FCSTD DOCUMENT  (FreeCAD 1.0R39109 (Git))
Label: CenterCoil
License: All rights reserved
LicenseURL: http://en.wikipedia.org/wiki/All_rights_reserved
objects: Sketcher::SketchObject×84, PartDesign::Pocket×55, PartDesign::Pad×22, PartDesign::PolarPattern×14, PartDesign::Body×10, App::Part×9, PartDesign::Chamfer×9, PartDesign::Fillet×8, PartDesign::Groove×5, Part::Feature×3, PartDesign::SubtractiveHelix×1
note: 509 computed .brp shape members not serialized (recipe doc carries the construction recipe); baked Part::Feature solids carry a one-line shape summary decoded from their .brp

FEATURE [Sketcher::SketchObject] Sketch
  ArcFitTolerance = 1e-06
  AttachmentSupport = -> [XY_Plane001]
  FullyConstrained = true
  MakeInternals = false
  MapMode = 5
  sketch-geometry (1):
    g0: Circle CenterX=0 CenterY=0 CenterZ=0 NormalX=0 NormalY=0 NormalZ=1 AngleXU=0 Radius=38.1
  constraints (2):
    c: Diameter(g0) = 76.2
    c: Coincident(g0,g-1)
FEATURE [PartDesign::Pad] Pad  label="CoilPad"
  Direction = (0,0,1)
  Length = 101.15
  Length2 = 10
  Profile = -> Sketch
  ReferenceAxis = -> Sketch [N_Axis]
  Suppressed = false
  Type = 0
FEATURE [Sketcher::SketchObject] Sketch001
  ArcFitTolerance = 1e-06
  AttachmentSupport = -> [XZ_Plane001]
  FullyConstrained = true
  MakeInternals = false
  MapMode = 5
  Placement = pos=(0,0,0) rot=(1,0,0;1.5708rad)
  sketch-geometry (1):
    g0: Circle CenterX=38.1 CenterY=4 CenterZ=0 NormalX=0 NormalY=0 NormalZ=1 AngleXU=0 Radius=1
  constraints (3):
    c: Diameter(g0) = 2
    c: DistanceX(g-1,g0) = 38.1
    c: DistanceY(g-1,g0) = 4
FEATURE [PartDesign::SubtractiveHelix] SubtractiveHelix
  Angle = 0
  Axis = (0,2e-16,1)
  Base = (0,0,0)
  BaseFeature = -> Pad
  Growth = 0
  HasBeenEdited = true
  Height = 93.15
  LeftHanded = false
  Mode = 0
  Outside = false
  Pitch = 2.3
  Profile = -> Sketch001
  ReferenceAxis = -> Sketch001 [V_Axis]
  Suppressed = false
  Tolerance = 0.1
  Turns = 40.5
FEATURE [Sketcher::SketchObject] Sketch002
  ArcFitTolerance = 1e-06
  AttachmentSupport = -> [SubtractiveHelix]
  FullyConstrained = true
  MakeInternals = false
  MapMode = 5
  Placement = pos=(0,0,101.15) rot=(0,0,1;0rad)
  sketch-geometry (1):
    g0: Circle CenterX=0 CenterY=0 CenterZ=0 NormalX=0 NormalY=0 NormalZ=1 AngleXU=0 Radius=23.1
  constraints (2):
    c: Diameter(g0) = 46.2
    c: Coincident(g0,g-1)
FEATURE [PartDesign::Pocket] Pocket  label="CenterPocket"
  BaseFeature = -> SubtractiveHelix
  Direction = (0,0,-1)
  Length = 5
  Length2 = 5
  Profile = -> Sketch002
  ReferenceAxis = -> Sketch002 [N_Axis]
  Suppressed = false
  Type = 1
FEATURE [Sketcher::SketchObject] Sketch003
  ArcFitTolerance = 1e-06
  AttachmentSupport = -> [Pocket]
  FullyConstrained = true
  MakeInternals = false
  MapMode = 5
  Placement = pos=(0,0,101.15) rot=(0,0,1;0rad)
  sketch-geometry (1):
    g0: Circle CenterX=0 CenterY=30.06 CenterZ=0 NormalX=0 NormalY=0 NormalZ=1 AngleXU=0 Radius=3.3
  constraints (3):
    c: Diameter(g0) = 6.6
    c: PointOnObject(g0,g-2)
    c: DistanceY(g-1,g0) = 30.06
FEATURE [PartDesign::Pocket] Pocket001  label="TopScrewPocket"
  BaseFeature = -> Pocket
  Direction = (0,0,-1)
  Length = 20
  Length2 = 5
  Profile = -> Sketch003
  ReferenceAxis = -> Sketch003 [N_Axis]
  Suppressed = false
  Type = 0
FEATURE [PartDesign::PolarPattern] PolarPattern  label="TopScrewPolarPattern"
  Angle = 360
  Axis = -> Sketch003 [N_Axis]
  BaseFeature = -> Pocket001
  Mode = 0
  Occurrences = 5
  Offset = 120
  Originals = -> [Pocket001]
  Suppressed = false
  TransformMode = 0
FEATURE [Sketcher::SketchObject] Sketch004
  ArcFitTolerance = 1e-06
  AttachmentSupport = -> [PolarPattern]
  FullyConstrained = true
  MakeInternals = false
  MapMode = 5
  Placement = pos=(0,0,0) rot=(1,0,0;3.14159rad)
  sketch-geometry (1):
    g0: Circle CenterX=0 CenterY=-30.03 CenterZ=0 NormalX=0 NormalY=0 NormalZ=1 AngleXU=0 Radius=3.3
  constraints (3):
    c: Diameter(g0) = 6.6
    c: PointOnObject(g0,g-2)
    c: DistanceY(g0,g-1) = 30.03
FEATURE [PartDesign::Pocket] Pocket002  label="BottomScrewPocket"
  BaseFeature = -> PolarPattern
  Direction = (0,0,1)
  Length = 20
  Length2 = 5
  Profile = -> Sketch004
  ReferenceAxis = -> Sketch004 [N_Axis]
  Suppressed = false
  Type = 0
FEATURE [PartDesign::PolarPattern] PolarPattern001  label="BottomScrewPolarPattern"
  Angle = 360
  Axis = -> Sketch004 [N_Axis]
  BaseFeature = -> Pocket002
  Mode = 0
  Occurrences = 5
  Offset = 120
  Originals = -> [Pocket002]
  Suppressed = false
  TransformMode = 0
FEATURE [Sketcher::SketchObject] Sketch005
  ArcFitTolerance = 1e-06
  AttachmentSupport = -> [PolarPattern001]
  FullyConstrained = true
  MakeInternals = false
  MapMode = 5
  Placement = pos=(0,0,101.15) rot=(0,0,1;0rad)
  sketch-geometry (4):
    g0: LineSegment StartX=-38.1 StartY=38.1 StartZ=0 EndX=-38.1 EndY=-38.1 EndZ=0
    g1: LineSegment StartX=-38.1 StartY=-38.1 StartZ=0 EndX=38.1 EndY=-38.1 EndZ=0
    g2: LineSegment StartX=38.1 StartY=-38.1 StartZ=0 EndX=38.1 EndY=38.1 EndZ=0
    g3: LineSegment StartX=38.1 StartY=38.1 StartZ=0 EndX=-38.1 EndY=38.1 EndZ=0
  constraints (11):
    c: Coincident(g0,g1)
    c: Coincident(g1,g2)
    c: Coincident(g2,g3)
    c: Coincident(g3,g0)
    c: Vertical(g0)
    c: Vertical(g2)
    c: Horizontal(g1)
    c: Horizontal(g3)
    c: Distance(g0,g2) = 76.2
    c: Distance(g1,g3) = 76.2
    c: Symmetric(g0,g1,g-1)
FEATURE [PartDesign::Pad] Pad001  label="TempPad"
  BaseFeature = -> PolarPattern001
  Direction = (0,0,1)
  Length = 10
  Length2 = 10
  Profile = -> Sketch005
  ReferenceAxis = -> Sketch005 [N_Axis]
  Suppressed = false
  Type = 0
FEATURE [Sketcher::SketchObject] Sketch006
  ArcFitTolerance = 1e-06
  AttachmentSupport = -> [Pad001]
  FullyConstrained = true
  MakeInternals = false
  MapMode = 5
  Placement = pos=(-38.1,0,0) rot=(0.57735,-0.57735,-0.57735;2.0944rad)
  sketch-geometry (1):
    g0: Circle CenterX=0 CenterY=97.15 CenterZ=0 NormalX=0 NormalY=0 NormalZ=1 AngleXU=0 Radius=1.05
  constraints (3):
    c: Diameter(g0) = 2.1
    c: PointOnObject(g0,g-2)
    c: DistanceY(g-1,g0) = 97.15
FEATURE [PartDesign::Pocket] Pocket003  label="TopWirePocket"
  BaseFeature = -> Pad001
  Direction = (1,0,0)
  Length = 16
  Length2 = 5
  Profile = -> Sketch006
  ReferenceAxis = -> Sketch006 [N_Axis]
  Suppressed = false
  Type = 0
FEATURE [Sketcher::SketchObject] Sketch007
  ArcFitTolerance = 1e-06
  AttachmentSupport = -> [Pocket003]
  FullyConstrained = true
  MakeInternals = false
  MapMode = 5
  Placement = pos=(38.1,0,0) rot=(0.57735,0.57735,0.57735;2.0944rad)
  sketch-geometry (1):
    g0: Circle CenterX=0 CenterY=4 CenterZ=0 NormalX=0 NormalY=0 NormalZ=1 AngleXU=0 Radius=1.05
  constraints (3):
    c: Diameter(g0) = 2.1
    c: PointOnObject(g0,g-2)
    c: DistanceY(g-1,g0) = 4
FEATURE [PartDesign::Pocket] Pocket004  label="BottomWirePocket"
  BaseFeature = -> Pocket003
  Direction = (-1,0,0)
  Length = 16
  Length2 = 5
  Profile = -> Sketch007
  ReferenceAxis = -> Sketch007 [N_Axis]
  Suppressed = false
  Type = 0
FEATURE [Sketcher::SketchObject] Sketch008
  ArcFitTolerance = 1e-06
  AttachmentSupport = -> [PolarPattern001]
  FullyConstrained = true
  MakeInternals = false
  MapMode = 5
  Placement = pos=(0,0,101.15) rot=(0,0,1;0rad)
  sketch-geometry (4):
    g0: LineSegment StartX=-38.1 StartY=38.1 StartZ=0 EndX=-38.1 EndY=-38.1 EndZ=0
    g1: LineSegment StartX=-38.1 StartY=-38.1 StartZ=0 EndX=38.1 EndY=-38.1 EndZ=0
    g2: LineSegment StartX=38.1 StartY=-38.1 StartZ=0 EndX=38.1 EndY=38.1 EndZ=0
    g3: LineSegment StartX=38.1 StartY=38.1 StartZ=0 EndX=-38.1 EndY=38.1 EndZ=0
  constraints (11):
    c: Coincident(g0,g1)
    c: Coincident(g1,g2)
    c: Coincident(g2,g3)
    c: Coincident(g3,g0)
    c: Vertical(g0)
    c: Vertical(g2)
    c: Horizontal(g1)
    c: Horizontal(g3)
    c: Distance(g0,g2) = 76.2
    c: Distance(g1,g3) = 76.2
    c: Symmetric(g0,g1,g-1)
FEATURE [PartDesign::Pocket] Pocket005  label="RemoveTempPad"
  BaseFeature = -> Pocket004
  Direction = (0,0,-1)
  Length = 10
  Length2 = 5
  Profile = -> Sketch008
  ReferenceAxis = -> Sketch008 [N_Axis]
  Reversed = true
  Suppressed = false
  Type = 0
FEATURE [PartDesign::Fillet] Fillet  label="WireFillet"
  Base = -> Pocket005 [Edge8,Edge9,Edge61]
  BaseFeature = -> Pocket005
  Radius = 4
  SupportTransform = false
  Suppressed = false
  UseAllEdges = false
FEATURE [PartDesign::Body] Body  label="CoilBody"
  AllowCompound = false
  Group = -> [Sketch,Pad,Sketch001,SubtractiveHelix,Sketch002,Pocket,Sketch003,Pocket001,PolarPattern,Sketch004,Pocket002,PolarPattern001,Sketch005,Pad001,Sketch006,Pocket003,Sketch007,Pocket004,Sketch008,Pocket005,Fillet]
  Origin = -> Origin001
  Tip = -> Fillet
FEATURE [App::Part] Part  label="CoilPart"
  Group = -> [Body]
  Origin = -> Origin
FEATURE [Sketcher::SketchObject] Sketch009
  ArcFitTolerance = 1e-06
  AttachmentSupport = -> [XY_Plane003]
  FullyConstrained = true
  MakeInternals = false
  MapMode = 5
  sketch-geometry (1):
    g0: Circle CenterX=0 CenterY=0 CenterZ=0 NormalX=0 NormalY=0 NormalZ=1 AngleXU=0 Radius=38.1
  constraints (2):
    c: Diameter(g0) = 76.2
    c: Coincident(g0,g-1)
FEATURE [PartDesign::Pad] Pad002  label="TopPlatePad"
  Direction = (0,0,1)
  Length = 30.575
  Length2 = 10
  Profile = -> Sketch009
  ReferenceAxis = -> Sketch009 [N_Axis]
  Suppressed = false
  Type = 0
FEATURE [Sketcher::SketchObject] Sketch011
  ArcFitTolerance = 1e-06
  FullyConstrained = true
  MakeInternals = false
  MapMode = 5
  Placement = pos=(0,0,30.575) rot=(0,0,1;0rad)
  sketch-geometry (1):
    g0: Circle CenterX=0 CenterY=30.06 CenterZ=0 NormalX=0 NormalY=0 NormalZ=1 AngleXU=0 Radius=5.5
  constraints (3):
    c: Diameter(g0) = 11
    c: PointOnObject(g0,g-2)
    c: DistanceY(g-1,g0) = 30.06
FEATURE [Sketcher::SketchObject] Sketch013
  ArcFitTolerance = 1e-06
  AttachmentSupport = -> [YZ_Plane003]
  FullyConstrained = true
  MakeInternals = false
  MapMode = 5
  Placement = pos=(0,0,0) rot=(0.57735,0.57735,0.57735;2.0944rad)
  sketch-geometry (5):
    g0: LineSegment StartX=10 StartY=33.721 StartZ=0 EndX=10 EndY=30.551 EndZ=0
    g1: LineSegment StartX=39.292 StartY=4 StartZ=0 EndX=45.437 EndY=4 EndZ=0
    g2: LineSegment StartX=45.437 StartY=4 StartZ=0 EndX=45.437 EndY=33.721 EndZ=0
    g3: LineSegment StartX=45.437 StartY=33.721 StartZ=0 EndX=10 EndY=33.721 EndZ=0
    g4: LineSegment StartX=10 StartY=30.551 StartZ=0 EndX=39.292 EndY=4 EndZ=0
  constraints (15):
    c: Vertical(g0)
    c: Coincident(g1,g2)
    c: Vertical(g2)
    c: Coincident(g2,g3)
    c: Coincident(g3,g0)
    c: Horizontal(g3)
    c: DistanceX(g-1,g0) = 10
    c: DistanceX(g-1,g1) = 45.437
    c: DistanceX(g1,g1) = 6.145
    c: DistanceY(g0,g0) = 3.17
    c: DistanceY(g-1,g2) = 33.721
    c: DistanceY(g-1,g1) = 4
    c: Coincident(g4,g0)
    c: Coincident(g4,g1)
    c: DistanceY(g-1,g1) = 4
FEATURE [PartDesign::PolarPattern] PolarPattern003
  Angle = 360
  Axis = -> Sketch011 [N_Axis]
  Mode = 0
  Occurrences = 5
  Offset = 120
  Suppressed = false
  TransformMode = 0
FEATURE [Sketcher::SketchObject] Sketch012
  ArcFitTolerance = 1e-06
  AttachmentSupport = -> [PolarPattern003]
  FullyConstrained = true
  MakeInternals = false
  MapMode = 5
  Placement = pos=(0,0,30.575) rot=(0,0,1;0rad)
  sketch-geometry (1):
    g0: Circle CenterX=0 CenterY=0 CenterZ=0 NormalX=0 NormalY=0 NormalZ=1 AngleXU=0 Radius=5
  constraints (2):
    c: Diameter(g0) = 10
    c: Coincident(g0,g-1)
FEATURE [PartDesign::Pocket] Pocket008  label="AntennaPocket"
  BaseFeature = -> Pad002
  Direction = (0,0,-1)
  Length = 5
  Length2 = 5
  Profile = -> Sketch012
  ReferenceAxis = -> Sketch012 [N_Axis]
  Suppressed = false
  Type = 1
FEATURE [PartDesign::Groove] Groove
  Angle = 360
  Angle2 = 60
  Axis = (0,0,1)
  Base = (0,0,0)
  BaseFeature = -> Pocket008
  Profile = -> Sketch013
  ReferenceAxis = -> Sketch013 [V_Axis]
  Suppressed = false
  Type = 0
FEATURE [Sketcher::SketchObject] Sketch014
  ArcFitTolerance = 1e-06
  AttachmentSupport = -> [Groove]
  FullyConstrained = true
  MakeInternals = false
  MapMode = 5
  Placement = pos=(0,0,30.575) rot=(0,0,1;0rad)
  sketch-geometry (6):
    g0: LineSegment StartX=-25.4 StartY=38.1 StartZ=0 EndX=25.4 EndY=38.1 EndZ=0
    g1: LineSegment StartX=25.4 StartY=38.1 StartZ=0 EndX=25.4 EndY=28.1 EndZ=0
    g2: LineSegment StartX=25.4 StartY=28.1 StartZ=0 EndX=7.5 EndY=6.5 EndZ=0
    g3: LineSegment StartX=7.5 StartY=6.5 StartZ=0 EndX=-7.5 EndY=6.5 EndZ=0
    g4: LineSegment StartX=-7.5 StartY=6.5 StartZ=0 EndX=-25.4 EndY=28.1 EndZ=0
    g5: LineSegment StartX=-25.4 StartY=28.1 StartZ=0 EndX=-25.4 EndY=38.1 EndZ=0
  constraints (18):
    c: Horizontal(g0)
    c: Coincident(g0,g1)
    c: Coincident(g1,g2)
    c: Coincident(g2,g3)
    c: Horizontal(g3)
    c: Coincident(g3,g4)
    c: Coincident(g4,g5)
    c: Coincident(g5,g0)
    c: Vertical(g5)
    c: DistanceX(g0,g0) = 50.8
    c: Parallel(g5,g1)
    c: DistanceX(g-1,g0) = 25.4
    c: DistanceY(g-1,g0) = 38.1
    c: DistanceY(g5,g5) = 10
    c: DistanceY(g1,g1) = 10
    c: DistanceX(g3,g3) = 15
    c: DistanceX(g-1,g2) = 7.5
    c: DistanceY(g-1,g2) = 6.5
FEATURE [PartDesign::Pad] Pad003  label="EdgePad"
  BaseFeature = -> Groove
  Direction = (0,0,1)
  Length = 30.575
  Length2 = 10
  Profile = -> Sketch014
  ReferenceAxis = -> Sketch014 [N_Axis]
  Reversed = true
  Suppressed = false
  Type = 0
FEATURE [Sketcher::SketchObject] Sketch019
  ArcFitTolerance = 1e-06
  AttachmentSupport = -> [YZ_Plane003]
  FullyConstrained = true
  MakeInternals = false
  MapMode = 5
  Placement = pos=(0,0,0) rot=(0.57735,0.57735,0.57735;2.0944rad)
  sketch-geometry (1):
    g0: Circle CenterX=-35.5 CenterY=0 CenterZ=0 NormalX=0 NormalY=0 NormalZ=1 AngleXU=0 Radius=1
  constraints (3):
    c: Diameter(g0) = 2
    c: PointOnObject(g0,g-1)
    c: DistanceX(g0,g-1) = 35.5
FEATURE [Sketcher::SketchObject] Sketch031
  ArcFitTolerance = 1e-06
  AttachmentSupport = -> [XY_Plane007]
  FullyConstrained = true
  MakeInternals = false
  MapMode = 5
  sketch-geometry (1):
    g0: Circle CenterX=0 CenterY=0 CenterZ=0 NormalX=0 NormalY=0 NormalZ=1 AngleXU=0 Radius=66.675
  constraints (2):
    c: Diameter(g0) = 133.35
    c: Coincident(g0,g-1)
FEATURE [PartDesign::Pad] Pad006  label="MainPad"
  Direction = (0,0,1)
  Length = 41
  Length2 = 10
  Profile = -> Sketch031
  ReferenceAxis = -> Sketch031 [N_Axis]
  Suppressed = false
  Type = 0
FEATURE [Sketcher::SketchObject] Sketch032
  ArcFitTolerance = 1e-06
  AttachmentSupport = -> [Pad006]
  FullyConstrained = true
  MakeInternals = false
  MapMode = 5
  Placement = pos=(0,0,41) rot=(0,0,1;0rad)
  sketch-geometry (4):
    g0: LineSegment StartX=-20.5 StartY=66.675 StartZ=0 EndX=-20.5 EndY=56.675 EndZ=0
    g1: LineSegment StartX=-20.5 StartY=56.675 StartZ=0 EndX=20.5 EndY=56.675 EndZ=0
    g2: LineSegment StartX=20.5 StartY=56.675 StartZ=0 EndX=20.5 EndY=66.675 EndZ=0
    g3: LineSegment StartX=20.5 StartY=66.675 StartZ=0 EndX=-20.5 EndY=66.675 EndZ=0
  constraints (12):
    c: Coincident(g0,g1)
    c: Coincident(g1,g2)
    c: Coincident(g2,g3)
    c: Coincident(g3,g0)
    c: Vertical(g0)
    c: Vertical(g2)
    c: Horizontal(g1)
    c: Horizontal(g3)
    c: Distance(g0,g2) = 41
    c: Distance(g1,g3) = 10
    c: DistanceY(g-1,g0) = 66.675
    c: DistanceX(g0,g-1) = 20.5
FEATURE [PartDesign::Pad] Pad007  label="EdgePad002"
  BaseFeature = -> Pad006
  Direction = (0,0,1)
  Length = 41
  Length2 = 10
  Profile = -> Sketch032
  ReferenceAxis = -> Sketch032 [N_Axis]
  Reversed = true
  Suppressed = false
  Type = 0
FEATURE [Sketcher::SketchObject] Sketch033
  ArcFitTolerance = 1e-06
  AttachmentSupport = -> [Pad007]
  FullyConstrained = true
  MakeInternals = false
  MapMode = 5
  Placement = pos=(0,66.675,0) rot=(0,0.707107,0.707107;3.14159rad)
  sketch-geometry (1):
    g0: Circle CenterX=0 CenterY=20.5 CenterZ=0 NormalX=0 NormalY=0 NormalZ=1 AngleXU=0 Radius=8.75
  constraints (3):
    c: Diameter(g0) = 17.5
    c: PointOnObject(g0,g-2)
    c: DistanceY(g-1,g0) = 20.5
FEATURE [Sketcher::SketchObject] Sketch036
  ArcFitTolerance = 1e-06
  FullyConstrained = true
  MakeInternals = false
  MapMode = 5
  Placement = pos=(0,0,41) rot=(0,0,1;0rad)
  sketch-geometry (4):
    g0: LineSegment StartX=0 StartY=47.1465 StartZ=0 EndX=-47.1462 EndY=0 EndZ=0
    g1: LineSegment StartX=-47.1462 StartY=0 StartZ=0 EndX=0 EndY=-47.1465 EndZ=0
    g2: LineSegment StartX=0 StartY=-47.1465 StartZ=0 EndX=47.1462 EndY=0 EndZ=0
    g3: LineSegment StartX=47.1462 StartY=0 StartZ=0 EndX=0 EndY=47.1465 EndZ=0
  constraints (12):
    c: PointOnObject(g0,g-2)
    c: Coincident(g0,g1)
    c: PointOnObject(g1,g-2)
    c: Coincident(g1,g2)
    c: PointOnObject(g2,g-1)
    c: Coincident(g2,g3)
    c: Coincident(g3,g0)
    c: Distance(g0) = 66.675
    c: Distance(g2) = 66.675
    c: Distance(g3) = 66.675
    c: Distance(g1) = 66.675
    c: DistanceY(g1,g0) = 94.293
FEATURE [Sketcher::SketchObject] Sketch040
  ArcFitTolerance = 1e-06
  FullyConstrained = true
  MakeInternals = false
  MapMode = 5
  Placement = pos=(0,0,41) rot=(0,0,1;0rad)
  sketch-geometry (1):
    g0: Circle CenterX=0 CenterY=0 CenterZ=0 NormalX=0 NormalY=0 NormalZ=1 AngleXU=0 Radius=50.675
  constraints (2):
    c: Diameter(g0) = 101.35
    c: Coincident(g0,g-1)
FEATURE [Sketcher::SketchObject] Sketch041
  ArcFitTolerance = 1e-06
  FullyConstrained = true
  MakeInternals = false
  MapMode = 5
  Placement = pos=(0,0,41) rot=(0,0,1;0rad)
  sketch-geometry (1):
    g0: Circle CenterX=0 CenterY=-58.675 CenterZ=0 NormalX=0 NormalY=0 NormalZ=1 AngleXU=0 Radius=3.675
  constraints (3):
    c: Diameter(g0) = 7.35
    c: PointOnObject(g0,g-2)
    c: DistanceY(g0,g-1) = 58.675
FEATURE [Sketcher::SketchObject] Sketch046
  ArcFitTolerance = 1e-06
  AttachmentSupport = -> [XY_Plane009]
  FullyConstrained = true
  MakeInternals = false
  MapMode = 5
  sketch-geometry (1):
    g0: Circle CenterX=0 CenterY=0 CenterZ=0 NormalX=0 NormalY=0 NormalZ=1 AngleXU=0 Radius=66.675
  constraints (2):
    c: Diameter(g0) = 133.35
    c: Coincident(g0,g-1)
FEATURE [PartDesign::Pad] Pad009  label="CoverPad"
  Direction = (0,0,1)
  Length = 47
  Length2 = 10
  Profile = -> Sketch046
  ReferenceAxis = -> Sketch046 [N_Axis]
  Suppressed = false
  Type = 0
FEATURE [Sketcher::SketchObject] Sketch047
  ArcFitTolerance = 1e-06
  AttachmentSupport = -> [Pad009]
  FullyConstrained = true
  MakeInternals = false
  MapMode = 5
  Placement = pos=(0,0,47) rot=(0,0,1;0rad)
  sketch-geometry (4):
    g0: LineSegment StartX=-20.5 StartY=66.675 StartZ=0 EndX=-20.5 EndY=56.675 EndZ=0
    g1: LineSegment StartX=-20.5 StartY=56.675 StartZ=0 EndX=20.5 EndY=56.675 EndZ=0
    g2: LineSegment StartX=20.5 StartY=56.675 StartZ=0 EndX=20.5 EndY=66.675 EndZ=0
    g3: LineSegment StartX=20.5 StartY=66.675 StartZ=0 EndX=-20.5 EndY=66.675 EndZ=0
  constraints (12):
    c: Coincident(g0,g1)
    c: Coincident(g1,g2)
    c: Coincident(g2,g3)
    c: Coincident(g3,g0)
    c: Vertical(g0)
    c: Vertical(g2)
    c: Horizontal(g1)
    c: Horizontal(g3)
    c: Distance(g0,g2) = 41
    c: Distance(g1,g3) = 10
    c: DistanceY(g-1,g0) = 66.675
    c: DistanceX(g0,g-1) = 20.5
FEATURE [PartDesign::Pad] Pad010  label="EdgePad003"
  BaseFeature = -> Pad009
  Direction = (0,0,1)
  Length = 47
  Length2 = 10
  Profile = -> Sketch047
  ReferenceAxis = -> Sketch047 [N_Axis]
  Reversed = true
  Suppressed = false
  Type = 0
FEATURE [Sketcher::SketchObject] Sketch048
  ArcFitTolerance = 1e-06
  AttachmentSupport = -> [Pad010]
  FullyConstrained = true
  MakeInternals = false
  MapMode = 5
  Placement = pos=(0,0,47) rot=(0,0,1;0rad)
  sketch-geometry (1):
    g0: Circle CenterX=0 CenterY=-58.675 CenterZ=0 NormalX=0 NormalY=0 NormalZ=1 AngleXU=0 Radius=3.675
  constraints (3):
    c: Diameter(g0) = 7.35
    c: PointOnObject(g0,g-2)
    c: DistanceY(g0,g-1) = 58.675
FEATURE [PartDesign::Pocket] Pocket034  label="ScrewPocket002"
  BaseFeature = -> Pad010
  Direction = (0,0,-1)
  Length = 5
  Length2 = 5
  Profile = -> Sketch048
  ReferenceAxis = -> Sketch048 [N_Axis]
  Suppressed = false
  Type = 1
FEATURE [PartDesign::PolarPattern] PolarPattern012
  Angle = 360
  Axis = -> Sketch048 [N_Axis]
  BaseFeature = -> Pocket034
  Mode = 0
  Occurrences = 3
  Offset = 120
  Originals = -> [Pocket034]
  Suppressed = false
  TransformMode = 0
FEATURE [Sketcher::SketchObject] Sketch049
  ArcFitTolerance = 1e-06
  AttachmentSupport = -> [PolarPattern012]
  FullyConstrained = true
  MakeInternals = false
  MapMode = 5
  Placement = pos=(0,0,47) rot=(0,0,1;0rad)
  sketch-geometry (1):
    g0: Circle CenterX=0 CenterY=-58.675 CenterZ=0 NormalX=0 NormalY=0 NormalZ=1 AngleXU=0 Radius=8.5
  constraints (3):
    c: Diameter(g0) = 17
    c: PointOnObject(g0,g-2)
    c: DistanceY(g0,g-1) = 58.675
FEATURE [PartDesign::Pocket] Pocket035  label="NutPocket002"
  BaseFeature = -> PolarPattern012
  Direction = (0,0,-1)
  Length = 43
  Length2 = 5
  Profile = -> Sketch049
  ReferenceAxis = -> Sketch049 [N_Axis]
  Suppressed = false
  Type = 0
FEATURE [PartDesign::PolarPattern] PolarPattern013
  Angle = 360
  Axis = -> Sketch049 [N_Axis]
  BaseFeature = -> Pocket035
  Mode = 0
  Occurrences = 3
  Offset = 120
  Originals = -> [Pocket035]
  Suppressed = false
  TransformMode = 0
FEATURE [Sketcher::SketchObject] Sketch050
  ArcFitTolerance = 1e-06
  AttachmentSupport = -> [YZ_Plane009]
  FullyConstrained = true
  MakeInternals = false
  MapMode = 5
  Placement = pos=(0,0,0) rot=(0.57735,0.57735,0.57735;2.0944rad)
  sketch-geometry (6):
    g0: LineSegment StartX=-20 StartY=55.851 StartZ=0 EndX=-20 EndY=47 EndZ=0
    g1: LineSegment StartX=-20 StartY=47 StartZ=0 EndX=-66.675 EndY=4 EndZ=0
    g2: LineSegment StartX=-66.675 StartY=38.14 StartZ=0 EndX=-20 EndY=55.851 EndZ=0
    g3: LineSegment StartX=-66.675 StartY=4 StartZ=0 EndX=-78.694 EndY=4 EndZ=0
    g4: LineSegment StartX=-78.694 StartY=4 StartZ=0 EndX=-78.694 EndY=38.14 EndZ=0
    g5: LineSegment StartX=-78.694 StartY=38.14 StartZ=0 EndX=-66.675 EndY=38.14 EndZ=0
  constraints (18):
    c: Vertical(g0)
    c: Coincident(g0,g1)
    c: Coincident(g2,g0)
    c: DistanceX(g0,g-1) = 20
    c: DistanceX(g1,g-1) = 66.675
    c: DistanceY(g-1,g0) = 47
    c: DistanceY(g-1,g1) = 4
    c: DistanceY(g1,g2) = 34.14
    c: DistanceY(g0,g0) = 8.851
    c: Coincident(g1,g3)
    c: Horizontal(g3)
    c: Coincident(g3,g4)
    c: Vertical(g4)
    c: Coincident(g4,g5)
    c: Coincident(g5,g2)
    c: Horizontal(g5)
    c: DistanceX(g5,g5) = 12.019
    c: DistanceX(g3,g3) = 12.019
FEATURE [Sketcher::SketchObject] Sketch053
  ArcFitTolerance = 1e-06
  AttachmentSupport = -> [XY_Plane011]
  FullyConstrained = true
  MakeInternals = false
  MapMode = 5
  sketch-geometry (1):
    g0: Circle CenterX=0 CenterY=0 CenterZ=0 NormalX=0 NormalY=0 NormalZ=1 AngleXU=0 Radius=38.1
  constraints (2):
    c: Diameter(g0) = 76.2
    c: Coincident(g0,g-1)
FEATURE [PartDesign::Pad] Pad011  label="TopPlatePad001"
  Direction = (0,0,1)
  Length = 47
  Length2 = 10
  Profile = -> Sketch053
  ReferenceAxis = -> Sketch053 [N_Axis]
  Suppressed = false
  Type = 0
FEATURE [Sketcher::SketchObject] Sketch054
  ArcFitTolerance = 1e-06
  AttachmentSupport = -> [Pad011]
  FullyConstrained = true
  MakeInternals = false
  MapMode = 5
  Placement = pos=(0,0,0) rot=(1,0,0;3.14159rad)
  sketch-geometry (1):
    g0: Circle CenterX=0 CenterY=30.06 CenterZ=0 NormalX=0 NormalY=0 NormalZ=1 AngleXU=0 Radius=2.75
  constraints (3):
    c: Diameter(g0) = 5.5
    c: PointOnObject(g0,g-2)
    c: DistanceY(g-1,g0) = 30.06
FEATURE [Sketcher::SketchObject] Sketch056
  ArcFitTolerance = 1e-06
  AttachmentSupport = -> [Pad011]
  FullyConstrained = true
  MakeInternals = false
  MapMode = 5
  Placement = pos=(0,0,47) rot=(0,0,1;0rad)
  sketch-geometry (1):
    g0: Circle CenterX=0 CenterY=0 CenterZ=0 NormalX=0 NormalY=0 NormalZ=1 AngleXU=0 Radius=7.25
  constraints (2):
    c: Diameter(g0) = 14.5
    c: Coincident(g0,g-1)
FEATURE [Sketcher::SketchObject] Sketch057
  ArcFitTolerance = 1e-06
  AttachmentSupport = -> [YZ_Plane011]
  FullyConstrained = true
  MakeInternals = false
  MapMode = 5
  Placement = pos=(0,0,0) rot=(0.57735,0.57735,0.57735;2.0944rad)
  sketch-geometry (5):
    g0: LineSegment StartX=12 StartY=47 StartZ=0 EndX=12 EndY=47 EndZ=0
    g1: LineSegment StartX=38.1 StartY=4 StartZ=0 EndX=45.437 EndY=4 EndZ=0
    g2: LineSegment StartX=45.437 StartY=4 StartZ=0 EndX=45.437 EndY=47 EndZ=0
    g3: LineSegment StartX=45.437 StartY=47 StartZ=0 EndX=12 EndY=47 EndZ=0
    g4: LineSegment StartX=12 StartY=47 StartZ=0 EndX=38.1 EndY=4 EndZ=0
  constraints (15):
    c: Vertical(g0)
    c: Coincident(g1,g2)
    c: Vertical(g2)
    c: Coincident(g2,g3)
    c: Coincident(g3,g0)
    c: Horizontal(g3)
    c: Coincident(g4,g0)
    c: Coincident(g4,g1)
    c: DistanceX(g-1,g1) = 38.1
    c: DistanceY(g1,g1) = 0
    c: DistanceY(g-1,g1) = 4
    c: DistanceY(g-1,g0) = 47
    c: DistanceX(g-1,g0) = 12
    c: DistanceY(g0,g0) = 0
    c: DistanceX(g-1,g2) = 45.437
FEATURE [Sketcher::SketchObject] Sketch063
  ArcFitTolerance = 1e-06
  AttachmentSupport = -> [YZ_Plane011]
  FullyConstrained = true
  MakeInternals = false
  MapMode = 5
  Placement = pos=(0,0,0) rot=(0.57735,0.57735,0.57735;2.0944rad)
  sketch-geometry (1):
    g0: Circle CenterX=-35.5 CenterY=0 CenterZ=0 NormalX=0 NormalY=0 NormalZ=1 AngleXU=0 Radius=1
  constraints (3):
    c: Diameter(g0) = 2
    c: PointOnObject(g0,g-1)
    c: DistanceX(g0,g-1) = 35.5
FEATURE [PartDesign::Groove] Groove005
  Angle = 360
  Angle2 = 60
  Axis = (0,0,1)
  Base = (0,0,0)
  BaseFeature = -> Pad011
  Profile = -> Sketch057
  ReferenceAxis = -> Sketch057 [V_Axis]
  Suppressed = false
  Type = 0
FEATURE [Sketcher::SketchObject] Sketch058
  ArcFitTolerance = 1e-06
  AttachmentSupport = -> [Groove005]
  FullyConstrained = true
  MakeInternals = false
  MapMode = 5
  Placement = pos=(0,0,0) rot=(1,0,0;3.14159rad)
  sketch-geometry (6):
    g0: LineSegment StartX=-25.4 StartY=38.1 StartZ=0 EndX=25.4 EndY=38.1 EndZ=0
    g1: LineSegment StartX=25.4 StartY=38.1 StartZ=0 EndX=25.4 EndY=28.1 EndZ=0
    g2: LineSegment StartX=25.4 StartY=28.1 StartZ=0 EndX=7.5 EndY=7.5 EndZ=0
    g3: LineSegment StartX=7.5 StartY=7.5 StartZ=0 EndX=-7.5 EndY=7.5 EndZ=0
    g4: LineSegment StartX=-7.5 StartY=7.5 StartZ=0 EndX=-25.4 EndY=28.1 EndZ=0
    g5: LineSegment StartX=-25.4 StartY=28.1 StartZ=0 EndX=-25.4 EndY=38.1 EndZ=0
  constraints (18):
    c: Horizontal(g0)
    c: Coincident(g0,g1)
    c: Coincident(g1,g2)
    c: Coincident(g2,g3)
    c: Horizontal(g3)
    c: Coincident(g3,g4)
    c: Coincident(g4,g5)
    c: Coincident(g5,g0)
    c: Vertical(g5)
    c: DistanceX(g0,g0) = 50.8
    c: Parallel(g5,g1)
    c: DistanceX(g-1,g0) = 25.4
    c: DistanceY(g-1,g0) = 38.1
    c: DistanceY(g5,g5) = 10
    c: DistanceY(g1,g1) = 10
    c: DistanceX(g3,g3) = 15
    c: DistanceX(g-1,g2) = 7.5
    c: DistanceY(g-1,g2) = 7.5
FEATURE [PartDesign::Pad] Pad012  label="EdgePad004"
  BaseFeature = -> Groove005
  Direction = (0,0,-1)
  Length = 30.6
  Length2 = 10
  Profile = -> Sketch058
  ReferenceAxis = -> Sketch058 [N_Axis]
  Reversed = true
  Suppressed = false
  Type = 0
FEATURE [Sketcher::SketchObject] Sketch059
  ArcFitTolerance = 1e-06
  AttachmentSupport = -> [Pad012]
  FullyConstrained = true
  MakeInternals = false
  MapMode = 5
  Placement = pos=(0,-38.1,0) rot=(1,0,0;1.5708rad)
  sketch-geometry (4):
    g0: Circle CenterX=-19 CenterY=26.075 CenterZ=0 NormalX=0 NormalY=0 NormalZ=1 AngleXU=0 Radius=2.15
    g1: Circle CenterX=19 CenterY=26.075 CenterZ=0 NormalX=0 NormalY=0 NormalZ=1 AngleXU=0 Radius=2.15
    g2: Circle CenterX=19 CenterY=4.5 CenterZ=0 NormalX=0 NormalY=0 NormalZ=1 AngleXU=0 Radius=2.15
    g3: Circle CenterX=-19 CenterY=4.5 CenterZ=0 NormalX=0 NormalY=0 NormalZ=1 AngleXU=0 Radius=2.15
  constraints (12):
    c: Equal(g0,g1)
    c: Equal(g0,g2)
    c: Equal(g0,g3)
    c: Diameter(g0) = 4.3
    c: DistanceY(g1,g0) = 0
    c: DistanceY(g2,g3) = 0
    c: DistanceX(g0,g3) = 0
    c: DistanceX(g2,g1) = 0
    c: DistanceX(g-1,g2) = 19
    c: DistanceX(g3,g-1) = 19
    c: DistanceY(g-1,g2) = 4.5
    c: DistanceY(g-1,g0) = 26.075
FEATURE [PartDesign::Pocket] Pocket041  label="EdgeScrewPockets001"
  BaseFeature = -> Pad012
  Direction = (0,1,-2e-16)
  Length = 10
  Length2 = 5
  Profile = -> Sketch059
  ReferenceAxis = -> Sketch059 [N_Axis]
  Suppressed = false
  Type = 0
FEATURE [Sketcher::SketchObject] Sketch060
  ArcFitTolerance = 1e-06
  AttachmentSupport = -> [Pocket041]
  FullyConstrained = true
  MakeInternals = false
  MapMode = 5
  Placement = pos=(0,0,0) rot=(1,0,0;3.14159rad)
  sketch-geometry (7):
    g0: LineSegment StartX=-11 StartY=0 StartZ=0 EndX=-5.5 EndY=-9.52628 EndZ=0
    g1: LineSegment StartX=-5.5 StartY=-9.52628 StartZ=0 EndX=5.5 EndY=-9.52628 EndZ=0
    g2: LineSegment StartX=5.5 StartY=-9.52628 StartZ=0 EndX=11 EndY=1.8e-15 EndZ=0
    g3: LineSegment StartX=11 StartY=1.8e-15 StartZ=0 EndX=5.5 EndY=9.52628 EndZ=0
    g4: LineSegment StartX=5.5 StartY=9.52628 StartZ=0 EndX=-5.5 EndY=9.52628 EndZ=0
    g5: LineSegment StartX=-5.5 StartY=9.52628 StartZ=0 EndX=-11 EndY=0 EndZ=0
    g6: Circle [constr] CenterX=0 CenterY=0 CenterZ=0 NormalX=0 NormalY=0 NormalZ=1 AngleXU=0 Radius=11
  constraints (16):
    c: Coincident(g0,g1)
    c: Coincident(g1,g2)
    c: Coincident(g2,g3)
    c: Coincident(g3,g4)
    c: Coincident(g4,g5)
    c: Coincident(g5,g0)
    c: Equal(g0, g1-g5) x5
    c: PointOnObject(g0,g6)
    c: PointOnObject(g1,g6)
    c: PointOnObject(g2,g6)
    c: PointOnObject(g3,g6)
    c: PointOnObject(g4,g6)
    c: PointOnObject(g5,g6)
    c: Radius(g6) = 11
    c: Coincident(g6,g-1)
    c: PointOnObject(g5,g-1)
FEATURE [PartDesign::Pocket] Pocket042  label="GiantNutPocket"
  BaseFeature = -> Pocket041
  Direction = (0,0,1)
  Length = 45
  Length2 = 5
  Profile = -> Sketch060
  ReferenceAxis = -> Sketch060 [N_Axis]
  Suppressed = false
  Type = 0
FEATURE [Sketcher::SketchObject] Sketch062
  ArcFitTolerance = 1e-06
  AttachmentSupport = -> [Pocket042]
  FullyConstrained = true
  MakeInternals = false
  MapMode = 5
  Placement = pos=(-25.4,0,0) rot=(0.57735,-0.57735,-0.57735;2.0944rad)
  sketch-geometry (1):
    g0: Circle CenterX=33.1 CenterY=15.2875 CenterZ=0 NormalX=0 NormalY=0 NormalZ=1 AngleXU=0 Radius=2.15
  constraints (3):
    c: Diameter(g0) = 4.3
    c: DistanceY(g-1,g0) = 15.2875
    c: DistanceX(g-1,g0) = 33.1
FEATURE [PartDesign::Pocket] Pocket043  label="SideEdgePocket"
  BaseFeature = -> Pocket042
  Direction = (1,0,0)
  Length = 5
  Length2 = 5
  Profile = -> Sketch062
  ReferenceAxis = -> Sketch062 [N_Axis]
  Suppressed = false
  Type = 1
FEATURE [PartDesign::Groove] Groove006  label="BottomGroove"
  Angle = 360
  Angle2 = 60
  Axis = (0,0,1)
  Base = (0,0,0)
  BaseFeature = -> Pocket043
  Profile = -> Sketch063
  ReferenceAxis = -> Sketch063 [V_Axis]
  Reversed = true
  Suppressed = false
  Type = 0
FEATURE [Sketcher::SketchObject] Sketch010
  ArcFitTolerance = 1e-06
  AttachmentSupport = -> [Groove006]
  FullyConstrained = true
  MakeInternals = false
  MapMode = 5
  Placement = pos=(0,0,0) rot=(1,0,0;3.14159rad)
  sketch-geometry (1):
    g0: Circle CenterX=0 CenterY=30.06 CenterZ=0 NormalX=0 NormalY=0 NormalZ=1 AngleXU=0 Radius=2.75
  constraints (3):
    c: Diameter(g0) = 5.5
    c: PointOnObject(g0,g-2)
    c: DistanceY(g-1,g0) = 30.06
FEATURE [PartDesign::Pocket] Pocket009  label="ScrewPocket"
  BaseFeature = -> Pad003
  Direction = (0,0,1)
  Length = 5
  Length2 = 5
  Profile = -> Sketch010
  ReferenceAxis = -> Sketch010 [N_Axis]
  Suppressed = false
  Type = 1
FEATURE [PartDesign::PolarPattern] PolarPattern004
  Angle = 360
  Axis = -> Sketch010 [N_Axis]
  BaseFeature = -> Pocket009
  Mode = 0
  Occurrences = 5
  Offset = 120
  Originals = -> [Pocket009]
  Suppressed = false
  TransformMode = 0
FEATURE [PartDesign::PolarPattern] PolarPattern005
  Angle = 360
  Axis = -> Sketch011 [N_Axis]
  BaseFeature = -> PolarPattern004
  Mode = 0
  Occurrences = 5
  Offset = 120
  Suppressed = false
  TransformMode = 0
FEATURE [Sketcher::SketchObject] Sketch015
  ArcFitTolerance = 1e-06
  AttachmentSupport = -> [PolarPattern005]
  FullyConstrained = true
  MakeInternals = false
  MapMode = 5
  Placement = pos=(0,38.1,0) rot=(0,0.707107,0.707107;3.14159rad)
  sketch-geometry (4):
    g0: Circle CenterX=-19 CenterY=26.075 CenterZ=0 NormalX=0 NormalY=0 NormalZ=1 AngleXU=0 Radius=2.15
    g1: Circle CenterX=19 CenterY=26.075 CenterZ=0 NormalX=0 NormalY=0 NormalZ=1 AngleXU=0 Radius=2.15
    g2: Circle CenterX=19 CenterY=4.5 CenterZ=0 NormalX=0 NormalY=0 NormalZ=1 AngleXU=0 Radius=2.15
    g3: Circle CenterX=-19 CenterY=4.5 CenterZ=0 NormalX=0 NormalY=0 NormalZ=1 AngleXU=0 Radius=2.15
  constraints (12):
    c: Equal(g0,g1)
    c: Equal(g0,g2)
    c: Equal(g0,g3)
    c: Diameter(g0) = 4.3
    c: DistanceY(g1,g0) = 0
    c: DistanceY(g2,g3) = 0
    c: DistanceX(g0,g3) = 0
    c: DistanceX(g2,g1) = 0
    c: DistanceX(g-1,g2) = 19
    c: DistanceX(g3,g-1) = 19
    c: DistanceY(g-1,g2) = 4.5
    c: DistanceY(g-1,g0) = 26.075
FEATURE [PartDesign::Pocket] Pocket011  label="EdgeScrewPockets"
  BaseFeature = -> PolarPattern005
  Direction = (0,-1,2e-16)
  Length = 10
  Length2 = 5
  Profile = -> Sketch015
  ReferenceAxis = -> Sketch015 [N_Axis]
  Suppressed = false
  Type = 0
FEATURE [PartDesign::Chamfer] Chamfer
  Angle = 45
  Base = -> Pocket011 [Edge58]
  BaseFeature = -> Pocket011
  ChamferType = 0
  FlipDirection = false
  Size = 2
  Size2 = 1
  SupportTransform = false
  Suppressed = false
  UseAllEdges = false
FEATURE [Sketcher::SketchObject] Sketch016
  ArcFitTolerance = 1e-06
  AttachmentSupport = -> [Chamfer]
  FullyConstrained = true
  MakeInternals = false
  MapMode = 5
  Placement = pos=(0,0,0) rot=(1,0,0;3.14159rad)
  sketch-geometry (7):
    g0: LineSegment StartX=-7.4 StartY=0 StartZ=0 EndX=-3.7 EndY=-6.40859 EndZ=0
    g1: LineSegment StartX=-3.7 StartY=-6.40859 StartZ=0 EndX=3.7 EndY=-6.40859 EndZ=0
    g2: LineSegment StartX=3.7 StartY=-6.40859 StartZ=0 EndX=7.4 EndY=1.64722e-11 EndZ=0
    g3: LineSegment StartX=7.4 StartY=1.64722e-11 StartZ=0 EndX=3.7 EndY=6.40859 EndZ=0
    g4: LineSegment StartX=3.7 StartY=6.40859 StartZ=0 EndX=-3.7 EndY=6.40859 EndZ=0
    g5: LineSegment StartX=-3.7 StartY=6.40859 StartZ=0 EndX=-7.4 EndY=0 EndZ=0
    g6: Circle [constr] CenterX=0 CenterY=0 CenterZ=0 NormalX=0 NormalY=0 NormalZ=1 AngleXU=0 Radius=7.4
  constraints (16):
    c: Coincident(g0,g1)
    c: Coincident(g1,g2)
    c: Coincident(g2,g3)
    c: Coincident(g3,g4)
    c: Coincident(g4,g5)
    c: Coincident(g5,g0)
    c: Equal(g0, g1-g5) x5
    c: PointOnObject(g0,g6)
    c: PointOnObject(g1,g6)
    c: PointOnObject(g2,g6)
    c: PointOnObject(g3,g6)
    c: PointOnObject(g4,g6)
    c: PointOnObject(g5,g6)
    c: Radius(g6) = 7.4
    c: Coincident(g6,g-1)
    c: PointOnObject(g5,g-1)
FEATURE [PartDesign::Pocket] Pocket012
  BaseFeature = -> Chamfer
  Direction = (0,0,1)
  Length = 28.575
  Length2 = 5
  Profile = -> Sketch016
  ReferenceAxis = -> Sketch016 [N_Axis]
  Suppressed = false
  Type = 0
FEATURE [Sketcher::SketchObject] Sketch017
  ArcFitTolerance = 1e-06
  AttachmentSupport = -> [Pocket012]
  FullyConstrained = true
  MakeInternals = false
  MapMode = 5
  Placement = pos=(0,0,0) rot=(1,0,0;3.14159rad)
  sketch-geometry (1):
    g0: Circle CenterX=7.3 CenterY=0 CenterZ=0 NormalX=0 NormalY=0 NormalZ=1 AngleXU=0 Radius=1
  constraints (3):
    c: Diameter(g0) = 2
    c: PointOnObject(g0,g-1)
    c: DistanceX(g-1,g0) = 7.3
FEATURE [PartDesign::Pocket] Pocket013
  BaseFeature = -> Pocket012
  Direction = (0,0,1)
  Length = 0.001
  Length2 = 5
  Profile = -> Sketch017
  ReferenceAxis = -> Sketch017 [N_Axis]
  Suppressed = false
  Type = 0
FEATURE [Sketcher::SketchObject] Sketch018
  ArcFitTolerance = 1e-06
  AttachmentSupport = -> [Pocket013]
  FullyConstrained = true
  MakeInternals = false
  MapMode = 5
  Placement = pos=(25.4,0,0) rot=(0.57735,0.57735,0.57735;2.0944rad)
  sketch-geometry (1):
    g0: Circle CenterX=33.1 CenterY=15.2875 CenterZ=0 NormalX=0 NormalY=0 NormalZ=1 AngleXU=0 Radius=2.15
  constraints (3):
    c: Diameter(g0) = 4.3
    c: DistanceY(g-1,g0) = 15.2875
    c: DistanceX(g-1,g0) = 33.1
FEATURE [PartDesign::Pocket] Pocket014
  BaseFeature = -> Pocket013
  Direction = (-1,0,0)
  Length = 5
  Length2 = 5
  Profile = -> Sketch018
  ReferenceAxis = -> Sketch018 [N_Axis]
  Suppressed = false
  Type = 1
FEATURE [PartDesign::Groove] Groove001
  Angle = 360
  Angle2 = 60
  Axis = (0,0,1)
  Base = (0,0,0)
  BaseFeature = -> Pocket014
  Profile = -> Sketch019
  ReferenceAxis = -> Sketch019 [V_Axis]
  Reversed = true
  Suppressed = false
  Type = 0
FEATURE [PartDesign::Body] Body001  label="TopPlateBody"
  AllowCompound = false
  Group = -> [Sketch009,Pad002,Sketch010,Sketch011,PolarPattern003,Sketch012,Pocket008,Sketch013,Groove,Sketch014,Pad003,Pocket009,PolarPattern004,PolarPattern005,Sketch015,Pocket011,Chamfer,Sketch016,Pocket012,Sketch017,Pocket013,Sketch018,Pocket014,Sketch019,Groove001]
  Origin = -> Origin003
  Tip = -> Groove001
FEATURE [App::Part] Part001  label="TopPlatePart"
  Group = -> [Body001]
  Origin = -> Origin002
FEATURE [PartDesign::Pocket] Pocket044  label="RodHolePocket"
  BaseFeature = -> Groove006
  Direction = (0,0,-1)
  Length = 5
  Length2 = 5
  Profile = -> Sketch056
  ReferenceAxis = -> Sketch056 [N_Axis]
  Suppressed = false
  Type = 1
FEATURE [PartDesign::Pocket] Pocket045  label="ScrewPocket003"
  BaseFeature = -> Pocket044
  Direction = (0,0,1)
  Length = 5
  Length2 = 5
  Profile = -> Sketch054
  ReferenceAxis = -> Sketch054 [N_Axis]
  Suppressed = false
  Type = 1
FEATURE [PartDesign::PolarPattern] PolarPattern014
  Angle = 360
  Axis = -> Sketch054 [N_Axis]
  BaseFeature = -> Pocket045
  Mode = 0
  Occurrences = 5
  Offset = 120
  Originals = -> [Pocket045]
  Suppressed = false
  TransformMode = 0
FEATURE [Sketcher::SketchObject] Sketch064
  ArcFitTolerance = 1e-06
  AttachmentSupport = -> [PolarPattern014]
  FullyConstrained = true
  MakeInternals = false
  MapMode = 5
  Placement = pos=(0,0,47) rot=(0,0,1;0rad)
  sketch-geometry (1):
    g0: Circle CenterX=0 CenterY=-30.06 CenterZ=0 NormalX=0 NormalY=0 NormalZ=1 AngleXU=0 Radius=5.5
  constraints (3):
    c: Diameter(g0) = 11
    c: PointOnObject(g0,g-2)
    c: DistanceY(g0,g-1) = 30.06
FEATURE [PartDesign::Pocket] Pocket046  label="NutPocket"
  BaseFeature = -> PolarPattern014
  Direction = (0,0,-1)
  Length = 43
  Length2 = 5
  Profile = -> Sketch064
  ReferenceAxis = -> Sketch064 [N_Axis]
  Suppressed = false
  Type = 0
FEATURE [PartDesign::PolarPattern] PolarPattern015
  Angle = 360
  Axis = -> Sketch064 [N_Axis]
  BaseFeature = -> Pocket046
  Mode = 0
  Occurrences = 5
  Offset = 120
  Originals = -> [Pocket046]
  Suppressed = false
  TransformMode = 0
FEATURE [Sketcher::SketchObject] Sketch065
  ArcFitTolerance = 1e-06
  AttachmentSupport = -> [PolarPattern015]
  FullyConstrained = true
  MakeInternals = false
  MapMode = 5
  Placement = pos=(0,0,0) rot=(1,0,0;3.14159rad)
  sketch-geometry (1):
    g0: Circle CenterX=0 CenterY=13.5 CenterZ=0 NormalX=0 NormalY=0 NormalZ=1 AngleXU=0 Radius=1.5
  constraints (3):
    c: Diameter(g0) = 3
    c: PointOnObject(g0,g-2)
    c: DistanceY(g-1,g0) = 13.5
FEATURE [PartDesign::Pocket] Pocket047  label="GluePocket"
  BaseFeature = -> PolarPattern015
  Direction = (0,0,1)
  Length = 3
  Length2 = 5
  Profile = -> Sketch065
  ReferenceAxis = -> Sketch065 [N_Axis]
  Suppressed = false
  Type = 0
FEATURE [PartDesign::PolarPattern] PolarPattern016
  Angle = 360
  Axis = -> Sketch065 [N_Axis]
  BaseFeature = -> Pocket047
  Mode = 0
  Occurrences = 6
  Offset = 120
  Originals = -> [Pocket047]
  Suppressed = false
  TransformMode = 0
FEATURE [PartDesign::Chamfer] Chamfer007
  Angle = 45
  Base = -> PolarPattern016 [Edge95,Edge96,Edge94,Edge86,Edge92,Edge87,Edge84,Edge93]
  BaseFeature = -> PolarPattern016
  ChamferType = 0
  FlipDirection = false
  Size = 2
  Size2 = 1
  SupportTransform = false
  Suppressed = false
  UseAllEdges = false
FEATURE [PartDesign::Body] Body005  label="TopPlateBody001"
  AllowCompound = false
  Group = -> [Sketch053,Pad011,Sketch054,Sketch056,Sketch057,Sketch058,Sketch059,Sketch060,Sketch062,Sketch063,Groove005,Pad012,Pocket041,Pocket042,Pocket043,Groove006,Pocket044,Pocket045,PolarPattern014,Sketch064,Pocket046,PolarPattern015,Sketch065,Pocket047,PolarPattern016,Chamfer007]
  Origin = -> Origin011
  Tip = -> Chamfer007
FEATURE [App::Part] Part005  label="BottomPlatePart"
  Group = -> [Body005]
  Origin = -> Origin010
FEATURE [PartDesign::Pocket] Pocket048  label="UHFMainPocket"
  BaseFeature = -> Pad007
  Direction = (0,-1,2e-16)
  Length = 16
  Length2 = 5
  Profile = -> Sketch033
  ReferenceAxis = -> Sketch033 [N_Axis]
  Suppressed = false
  Type = 0
FEATURE [Sketcher::SketchObject] Sketch034
  ArcFitTolerance = 1e-06
  AttachmentSupport = -> [Pocket048]
  FullyConstrained = true
  MakeInternals = false
  MapMode = 5
  Placement = pos=(0,66.675,0) rot=(0,0.707107,0.707107;3.14159rad)
  sketch-geometry (4):
    g0: LineSegment StartX=-12.75 StartY=33.25 StartZ=0 EndX=-12.75 EndY=7.75 EndZ=0
    g1: LineSegment StartX=-12.75 StartY=7.75 StartZ=0 EndX=12.75 EndY=7.75 EndZ=0
    g2: LineSegment StartX=12.75 StartY=7.75 StartZ=0 EndX=12.75 EndY=33.25 EndZ=0
    g3: LineSegment StartX=12.75 StartY=33.25 StartZ=0 EndX=-12.75 EndY=33.25 EndZ=0
  constraints (12):
    c: Coincident(g0,g1)
    c: Coincident(g1,g2)
    c: Coincident(g2,g3)
    c: Coincident(g3,g0)
    c: Vertical(g0)
    c: Vertical(g2)
    c: Horizontal(g1)
    c: Horizontal(g3)
    c: Distance(g0,g2) = 25.5
    c: Distance(g1,g3) = 25.5
    c: DistanceY(g-1,g0) = 7.75
    c: DistanceX(g0,g-1) = 12.75
FEATURE [PartDesign::Pocket] Pocket049  label="UHFBodyPocket"
  BaseFeature = -> Pocket048
  Direction = (0,-1,2e-16)
  Length = 2.3
  Length2 = 5
  Profile = -> Sketch034
  ReferenceAxis = -> Sketch034 [N_Axis]
  Suppressed = false
  Type = 0
FEATURE [Sketcher::SketchObject] Sketch035
  ArcFitTolerance = 1e-06
  AttachmentSupport = -> [Pocket049]
  FullyConstrained = true
  MakeInternals = false
  MapMode = 5
  Placement = pos=(0,64.375,-3.6e-14) rot=(0,0.707107,0.707107;3.14159rad)
  sketch-geometry (4):
    g0: Circle CenterX=-9.1 CenterY=29.6 CenterZ=0 NormalX=0 NormalY=0 NormalZ=1 AngleXU=0 Radius=1.7
    g1: Circle CenterX=9.1 CenterY=29.6 CenterZ=0 NormalX=0 NormalY=0 NormalZ=1 AngleXU=0 Radius=1.7
    g2: Circle CenterX=9.1 CenterY=11.4 CenterZ=0 NormalX=0 NormalY=0 NormalZ=1 AngleXU=0 Radius=1.7
    g3: Circle CenterX=-9.1 CenterY=11.4 CenterZ=0 NormalX=0 NormalY=0 NormalZ=1 AngleXU=0 Radius=1.7
  constraints (12):
    c: Equal(g0,g1)
    c: Equal(g0,g2)
    c: Equal(g0,g3)
    c: Diameter(g0) = 3.4
    c: DistanceX(g0,g3) = 0
    c: DistanceX(g2,g1) = 0
    c: DistanceY(g2,g3) = 0
    c: DistanceY(g1,g0) = 0
    c: DistanceY(g-1,g3) = 11.4
    c: DistanceX(g3,g-1) = 9.1
    c: DistanceX(g-1,g2) = 9.1
    c: DistanceY(g3,g0) = 18.2
FEATURE [PartDesign::Pocket] Pocket050  label="UHFBoltPockets"
  BaseFeature = -> Pocket049
  Direction = (0,-1,2e-16)
  Length = 16
  Length2 = 5
  Profile = -> Sketch035
  ReferenceAxis = -> Sketch035 [N_Axis]
  Suppressed = false
  Type = 0
FEATURE [PartDesign::Pocket] Pocket051  label="SquarePocket"
  BaseFeature = -> Pocket050
  Direction = (0,0,-1)
  Length = 37
  Length2 = 5
  Profile = -> Sketch036
  ReferenceAxis = -> Sketch036 [N_Axis]
  Suppressed = false
  Type = 0
FEATURE [Sketcher::SketchObject] Sketch037  label="SideRadialHole"
  ArcFitTolerance = 1e-06
  AttachmentSupport = -> [Pocket051]
  FullyConstrained = true
  MakeInternals = false
  MapMode = 5
  Placement = pos=(23.5732,-23.5731,0) rot=(-0.281086,0.678598,0.678598;3.68962rad)
  sketch-geometry (1):
    g0: Circle CenterX=0 CenterY=8.5 CenterZ=0 NormalX=0 NormalY=0 NormalZ=1 AngleXU=0 Radius=1.6
  constraints (3):
    c: Diameter(g0) = 3.2
    c: PointOnObject(g0,g-2)
    c: DistanceY(g-1,g0) = 8.5
FEATURE [PartDesign::Pocket] Pocket052  label="SideRadialPocket"
  BaseFeature = -> Pocket051
  Direction = (0.707109,-0.707104,-1e-16)
  Length = 5
  Length2 = 5
  Profile = -> Sketch037
  ReferenceAxis = -> Sketch037 [N_Axis]
  Suppressed = false
  Type = 1
FEATURE [PartDesign::PolarPattern] PolarPattern017
  Angle = 360
  Axis = -> Z_Axis007
  BaseFeature = -> Pocket052
  Mode = 0
  Occurrences = 4
  Offset = 120
  Originals = -> [Pocket052]
  Suppressed = false
  TransformMode = 0
FEATURE [Sketcher::SketchObject] Sketch039
  ArcFitTolerance = 1e-06
  AttachmentSupport = -> [PolarPattern017]
  FullyConstrained = true
  MakeInternals = false
  MapMode = 5
  Placement = pos=(23.5732,-23.5731,0) rot=(-0.281086,0.678598,0.678598;3.68962rad)
  sketch-geometry (7):
    g0: LineSegment StartX=2.8 StartY=8.5 StartZ=0 EndX=1.4 EndY=10.9249 EndZ=0
    g1: LineSegment StartX=1.4 StartY=10.9249 StartZ=0 EndX=-1.4 EndY=10.9249 EndZ=0
    g2: LineSegment StartX=-1.4 StartY=10.9249 StartZ=0 EndX=-2.8 EndY=8.5 EndZ=0
    g3: LineSegment StartX=-2.8 StartY=8.5 StartZ=0 EndX=-1.4 EndY=6.07513 EndZ=0
    g4: LineSegment StartX=-1.4 StartY=6.07513 StartZ=0 EndX=1.4 EndY=6.07513 EndZ=0
    g5: LineSegment StartX=1.4 StartY=6.07513 StartZ=0 EndX=2.8 EndY=8.5 EndZ=0
    g6: Circle [constr] CenterX=0 CenterY=8.5 CenterZ=0 NormalX=0 NormalY=0 NormalZ=1 AngleXU=0 Radius=2.8
  constraints (17):
    c: Coincident(g0,g1)
    c: Coincident(g1,g2)
    c: Coincident(g2,g3)
    c: Coincident(g3,g4)
    c: Coincident(g4,g5)
    c: Coincident(g5,g0)
    c: Equal(g0, g1-g5) x5
    c: PointOnObject(g0,g6)
    c: PointOnObject(g1,g6)
    c: PointOnObject(g2,g6)
    c: PointOnObject(g3,g6)
    c: PointOnObject(g4,g6)
    c: PointOnObject(g5,g6)
    c: Radius(g6) = 2.8
    c: PointOnObject(g6,g-2)
    c: DistanceY(g-1,g6) = 8.5
    c: DistanceY(g-1,g2) = 8.5
FEATURE [PartDesign::Pocket] Pocket053  label="SideRadialHexPocket"
  BaseFeature = -> PolarPattern017
  Direction = (0.707109,-0.707104,-1e-16)
  Length = 30
  Length2 = 5
  Profile = -> Sketch039
  ReferenceAxis = -> Sketch039 [N_Axis]
  Suppressed = false
  Type = 0
FEATURE [PartDesign::PolarPattern] PolarPattern018
  Angle = 360
  Axis = -> Z_Axis007
  BaseFeature = -> Pocket053
  Mode = 0
  Occurrences = 4
  Offset = 120
  Originals = -> [Pocket053]
  Suppressed = false
  TransformMode = 0
FEATURE [PartDesign::Pocket] Pocket054  label="CenterRoundPocket"
  BaseFeature = -> PolarPattern018
  Direction = (0,0,-1)
  Length = 37
  Length2 = 5
  Profile = -> Sketch040
  ReferenceAxis = -> Sketch040 [N_Axis]
  Suppressed = false
  Type = 0
FEATURE [PartDesign::Pocket] Pocket055  label="BoltPocket"
  BaseFeature = -> Pocket054
  Direction = (0,0,-1)
  Length = 5
  Length2 = 5
  Profile = -> Sketch041
  ReferenceAxis = -> Sketch041 [N_Axis]
  Suppressed = false
  Type = 1
FEATURE [PartDesign::PolarPattern] PolarPattern019
  Angle = 360
  Axis = -> Sketch041 [N_Axis]
  BaseFeature = -> Pocket055
  Mode = 0
  Occurrences = 3
  Offset = 120
  Originals = -> [Pocket055]
  Suppressed = false
  TransformMode = 0
FEATURE [Sketcher::SketchObject] Sketch042
  ArcFitTolerance = 1e-06
  AttachmentSupport = -> [PolarPattern019]
  FullyConstrained = true
  MakeInternals = false
  MapMode = 5
  Placement = pos=(0,0,4) rot=(0,0,1;0rad)
  sketch-geometry (1):
    g0: Circle CenterX=0 CenterY=0 CenterZ=0 NormalX=0 NormalY=0 NormalZ=1 AngleXU=0 Radius=22.5
  constraints (2):
    c: Diameter(g0) = 45
    c: Coincident(g0,g-1)
FEATURE [PartDesign::Pad] Pad013  label="InsidePad"
  BaseFeature = -> PolarPattern019
  Direction = (0,0,1)
  Length = 2
  Length2 = 10
  Profile = -> Sketch042
  ReferenceAxis = -> Sketch042 [N_Axis]
  Suppressed = false
  Type = 0
FEATURE [Sketcher::SketchObject] Sketch044
  ArcFitTolerance = 1e-06
  AttachmentSupport = -> [Pad013]
  FullyConstrained = true
  MakeInternals = false
  MapMode = 5
  Placement = pos=(0,0,6) rot=(0,0,1;0rad)
  sketch-geometry (1):
    g0: Circle CenterX=0 CenterY=0 CenterZ=0 NormalX=0 NormalY=0 NormalZ=1 AngleXU=0 Radius=7.25
  constraints (2):
    c: Diameter(g0) = 14.5
    c: Coincident(g0,g-1)
FEATURE [PartDesign::Pocket] Pocket056  label="BoltPocket001"
  BaseFeature = -> Pad013
  Direction = (0,0,-1)
  Length = 5
  Length2 = 5
  Profile = -> Sketch044
  ReferenceAxis = -> Sketch044 [N_Axis]
  Suppressed = false
  Type = 1
FEATURE [Sketcher::SketchObject] Sketch045
  ArcFitTolerance = 1e-06
  AttachmentSupport = -> [Pocket056]
  FullyConstrained = true
  MakeInternals = false
  MapMode = 5
  Placement = pos=(0,0,41) rot=(0,0,1;0rad)
  sketch-geometry (4):
    g0: LineSegment StartX=-14 StartY=52 StartZ=0 EndX=-14 EndY=42 EndZ=0
    g1: LineSegment StartX=-14 StartY=42 StartZ=0 EndX=14 EndY=42 EndZ=0
    g2: LineSegment StartX=14 StartY=42 StartZ=0 EndX=14 EndY=52 EndZ=0
    g3: LineSegment StartX=14 StartY=52 StartZ=0 EndX=-14 EndY=52 EndZ=0
  constraints (12):
    c: Coincident(g0,g1)
    c: Coincident(g1,g2)
    c: Coincident(g2,g3)
    c: Coincident(g3,g0)
    c: Vertical(g0)
    c: Vertical(g2)
    c: Horizontal(g1)
    c: Horizontal(g3)
    c: Distance(g0,g2) = 28
    c: Distance(g1,g3) = 10
    c: DistanceX(g0,g-1) = 14
    c: DistanceY(g-1,g0) = 52
FEATURE [PartDesign::Pocket] Pocket057  label="FlatPocket"
  BaseFeature = -> Pocket056
  Direction = (0,0,-1)
  Length = 37
  Length2 = 5
  Profile = -> Sketch045
  ReferenceAxis = -> Sketch045 [N_Axis]
  Suppressed = false
  Type = 0
FEATURE [PartDesign::Chamfer] Chamfer008
  Angle = 45
  Base = -> Pocket057 [Edge106]
  BaseFeature = -> Pocket057
  ChamferType = 0
  FlipDirection = false
  Size = 1
  Size2 = 1
  SupportTransform = false
  Suppressed = false
  UseAllEdges = false
FEATURE [PartDesign::Body] Body003  label="BottomGroundBody"
  AllowCompound = false
  Group = -> [Sketch031,Pad006,Sketch032,Pad007,Sketch033,Sketch034,Sketch035,Sketch036,Sketch037,Sketch039,Sketch040,Sketch041,Sketch042,Sketch044,Sketch045,Pocket048,Pocket049,Pocket050,Pocket051,Pocket052,PolarPattern017,Pocket053,PolarPattern018,Pocket054,Pocket055,PolarPattern019,Pad013,Pocket056,Pocket057,Chamfer008]
  Origin = -> Origin007
  Tip = -> Chamfer008
FEATURE [App::Part] Part003  label="BottomGround"
  Group = -> [Body003]
  Origin = -> Origin006
FEATURE [PartDesign::Groove] Groove007
  Angle = 360
  Angle2 = 60
  Axis = (0,0,1)
  Base = (0,0,0)
  BaseFeature = -> PolarPattern013
  Profile = -> Sketch050
  ReferenceAxis = -> Sketch050 [V_Axis]
  Reversed = true
  Suppressed = false
  Type = 0
FEATURE [Sketcher::SketchObject] Sketch051
  ArcFitTolerance = 1e-06
  AttachmentSupport = -> [Groove007]
  FullyConstrained = true
  MakeInternals = false
  MapMode = 5
  Placement = pos=(0,0,47) rot=(0,0,1;0rad)
  sketch-geometry (1):
    g0: Circle CenterX=0 CenterY=0 CenterZ=0 NormalX=0 NormalY=0 NormalZ=1 AngleXU=0 Radius=7.25
  constraints (2):
    c: Diameter(g0) = 14.5
    c: Coincident(g0,g-1)
FEATURE [PartDesign::Pocket] Pocket058  label="RodPocket"
  BaseFeature = -> Groove007
  Direction = (0,0,-1)
  Length = 5
  Length2 = 5
  Profile = -> Sketch051
  ReferenceAxis = -> Sketch051 [N_Axis]
  Suppressed = false
  Type = 1
FEATURE [Sketcher::SketchObject] Sketch052
  ArcFitTolerance = 1e-06
  AttachmentSupport = -> [Pocket058]
  FullyConstrained = true
  MakeInternals = false
  MapMode = 5
  Placement = pos=(0,0,0) rot=(1,0,0;3.14159rad)
  sketch-geometry (7):
    g0: LineSegment StartX=11 StartY=0 StartZ=0 EndX=5.5 EndY=9.52628 EndZ=0
    g1: LineSegment StartX=5.5 StartY=9.52628 StartZ=0 EndX=-5.5 EndY=9.52628 EndZ=0
    g2: LineSegment StartX=-5.5 StartY=9.52628 StartZ=0 EndX=-11 EndY=-1.8e-15 EndZ=0
    g3: LineSegment StartX=-11 StartY=-1.8e-15 StartZ=0 EndX=-5.5 EndY=-9.52628 EndZ=0
    g4: LineSegment StartX=-5.5 StartY=-9.52628 StartZ=0 EndX=5.5 EndY=-9.52628 EndZ=0
    g5: LineSegment StartX=5.5 StartY=-9.52628 StartZ=0 EndX=11 EndY=0 EndZ=0
    g6: Circle [constr] CenterX=0 CenterY=0 CenterZ=0 NormalX=0 NormalY=0 NormalZ=1 AngleXU=0 Radius=11
  constraints (16):
    c: Coincident(g0,g1)
    c: Coincident(g1,g2)
    c: Coincident(g2,g3)
    c: Coincident(g3,g4)
    c: Coincident(g4,g5)
    c: Coincident(g5,g0)
    c: Equal(g0, g1-g5) x5
    c: PointOnObject(g0,g6)
    c: PointOnObject(g1,g6)
    c: PointOnObject(g2,g6)
    c: PointOnObject(g3,g6)
    c: PointOnObject(g4,g6)
    c: PointOnObject(g5,g6)
    c: Radius(g6) = 11
    c: Coincident(g6,g-1)
    c: PointOnObject(g5,g-1)
FEATURE [PartDesign::Pocket] Pocket059
  BaseFeature = -> Pocket058
  Direction = (0,0,1)
  Length = 45
  Length2 = 5
  Profile = -> Sketch052
  ReferenceAxis = -> Sketch052 [N_Axis]
  Suppressed = false
  Type = 0
FEATURE [PartDesign::Chamfer] Chamfer009  label="GlueChamfer"
  Angle = 45
  Base = -> Pocket059 [Edge17,Edge16,Edge12,Edge13,Edge14,Edge15]
  BaseFeature = -> Pocket059
  ChamferType = 0
  FlipDirection = false
  Size = 2
  Size2 = 1
  SupportTransform = false
  Suppressed = false
  UseAllEdges = false
FEATURE [Sketcher::SketchObject] Sketch066
  ArcFitTolerance = 1e-06
  AttachmentSupport = -> [Chamfer009]
  FullyConstrained = true
  MakeInternals = false
  MapMode = 5
  Placement = pos=(0,0,0) rot=(1,0,0;3.14159rad)
  sketch-geometry (1):
    g0: Circle CenterX=0 CenterY=-14.2 CenterZ=0 NormalX=0 NormalY=0 NormalZ=1 AngleXU=0 Radius=1
  constraints (3):
    c: Diameter(g0) = 2
    c: PointOnObject(g0,g-2)
    c: DistanceY(g0,g-1) = 14.2
FEATURE [PartDesign::Pocket] Pocket060  label="GluePocket001"
  BaseFeature = -> Chamfer009
  Direction = (0,0,1)
  Length = 5
  Length2 = 5
  Profile = -> Sketch066
  ReferenceAxis = -> Sketch066 [N_Axis]
  Suppressed = false
  Type = 0
FEATURE [PartDesign::PolarPattern] PolarPattern020
  Angle = 360
  Axis = -> Sketch066 [N_Axis]
  BaseFeature = -> Pocket060
  Mode = 0
  Occurrences = 6
  Offset = 120
  Originals = -> [Pocket060]
  Suppressed = false
  TransformMode = 0
FEATURE [PartDesign::Body] Body004  label="BottomGroundBody001"
  AllowCompound = false
  Group = -> [Sketch046,Pad009,Sketch047,Pad010,Sketch048,Pocket034,PolarPattern012,Sketch049,Pocket035,PolarPattern013,Sketch050,Sketch051,Sketch052,Groove007,Pocket058,Pocket059,Chamfer009,Sketch066,Pocket060,PolarPattern020]
  Origin = -> Origin009
  Tip = -> PolarPattern020
FEATURE [App::Part] Part004  label="BottomGroundCover"
  Group = -> [Body004]
  Origin = -> Origin008
FEATURE [Sketcher::SketchObject] Sketch067
  ArcFitTolerance = 1e-06
  AttachmentSupport = -> [XY_Plane013]
  FullyConstrained = true
  MakeInternals = false
  MapMode = 5
  sketch-geometry (4):
    g0: LineSegment StartX=-25.4 StartY=15.3 StartZ=0 EndX=-25.4 EndY=-15.3 EndZ=0
    g1: LineSegment StartX=-25.4 StartY=-15.3 StartZ=0 EndX=25.4 EndY=-15.3 EndZ=0
    g2: LineSegment StartX=25.4 StartY=-15.3 StartZ=0 EndX=25.4 EndY=15.3 EndZ=0
    g3: LineSegment StartX=25.4 StartY=15.3 StartZ=0 EndX=-25.4 EndY=15.3 EndZ=0
  constraints (11):
    c: Coincident(g0,g1)
    c: Coincident(g1,g2)
    c: Coincident(g2,g3)
    c: Coincident(g3,g0)
    c: Vertical(g0)
    c: Vertical(g2)
    c: Horizontal(g1)
    c: Horizontal(g3)
    c: Distance(g0,g2) = 50.8
    c: Distance(g1,g3) = 30.6
    c: Symmetric(g0,g1,g-1)
FEATURE [PartDesign::Pad] Pad014  label="BasePad"
  Direction = (0,0,1)
  Length = 4
  Length2 = 10
  Profile = -> Sketch067
  ReferenceAxis = -> Sketch067 [N_Axis]
  Suppressed = false
  Type = 0
FEATURE [Sketcher::SketchObject] Sketch068
  ArcFitTolerance = 1e-06
  AttachmentSupport = -> [Pad014]
  FullyConstrained = true
  MakeInternals = false
  MapMode = 5
  Placement = pos=(0,0,4) rot=(0,0,1;0rad)
  sketch-geometry (4):
    g0: Circle CenterX=19 CenterY=10.8 CenterZ=0 NormalX=0 NormalY=0 NormalZ=1 AngleXU=0 Radius=1.6
    g1: Circle CenterX=19 CenterY=-10.8 CenterZ=0 NormalX=0 NormalY=0 NormalZ=1 AngleXU=0 Radius=1.6
    g2: Circle CenterX=-19 CenterY=-10.8 CenterZ=0 NormalX=0 NormalY=0 NormalZ=1 AngleXU=0 Radius=1.6
    g3: Circle CenterX=-19 CenterY=10.8 CenterZ=0 NormalX=0 NormalY=0 NormalZ=1 AngleXU=0 Radius=1.6
  constraints (12):
    c: Diameter(g0) = 3.2
    c: Diameter(g1) = 3.2
    c: Diameter(g2) = 3.2
    c: Diameter(g3) = 3.2
    c: DistanceY(g2,g1) = 0
    c: DistanceY(g0,g3) = 0
    c: DistanceX(g3,g2) = 0
    c: DistanceX(g0,g1) = 0
    c: DistanceX(g2,g-1) = 19
    c: DistanceX(g-1,g1) = 19
    c: DistanceY(g1,g-1) = 10.8
    c: DistanceY(g-1,g3) = 10.8
FEATURE [PartDesign::Pocket] Pocket061  label="ScrewPockets"
  BaseFeature = -> Pad014
  Direction = (0,0,-1)
  Length = 5
  Length2 = 5
  Profile = -> Sketch068
  ReferenceAxis = -> Sketch068 [N_Axis]
  Suppressed = false
  Type = 1
FEATURE [Sketcher::SketchObject] Sketch069
  ArcFitTolerance = 1e-06
  AttachmentSupport = -> [Pocket061]
  FullyConstrained = true
  MakeInternals = false
  MapMode = 5
  Placement = pos=(0,0,4) rot=(0,0,1;0rad)
  sketch-geometry (4):
    g0: LineSegment StartX=-25.4 StartY=6 StartZ=0 EndX=-25.4 EndY=-6 EndZ=0
    g1: LineSegment StartX=-25.4 StartY=-6 StartZ=0 EndX=25.4 EndY=-6 EndZ=0
    g2: LineSegment StartX=25.4 StartY=-6 StartZ=0 EndX=25.4 EndY=6 EndZ=0
    g3: LineSegment StartX=25.4 StartY=6 StartZ=0 EndX=-25.4 EndY=6 EndZ=0
  constraints (11):
    c: Coincident(g0,g1)
    c: Coincident(g1,g2)
    c: Coincident(g2,g3)
    c: Coincident(g3,g0)
    c: Vertical(g0)
    c: Vertical(g2)
    c: Horizontal(g1)
    c: Horizontal(g3)
    c: Distance(g0,g2) = 50.8
    c: Distance(g1,g3) = 12
    c: Symmetric(g0,g1,g-1)
FEATURE [PartDesign::Pad] Pad015
  BaseFeature = -> Pocket061
  Direction = (0,0,1)
  Length = 25
  Length2 = 10
  Profile = -> Sketch069
  ReferenceAxis = -> Sketch069 [N_Axis]
  Suppressed = false
  Type = 0
FEATURE [Sketcher::SketchObject] Sketch070
  ArcFitTolerance = 1e-06
  AttachmentSupport = -> [Pad015]
  FullyConstrained = true
  MakeInternals = false
  MapMode = 5
  Placement = pos=(0,6,0) rot=(0,0.707107,0.707107;3.14159rad)
  sketch-geometry (1):
    g0: Circle CenterX=12.9 CenterY=16.5 CenterZ=0 NormalX=0 NormalY=0 NormalZ=1 AngleXU=0 Radius=4.85
  constraints (3):
    c: Diameter(g0) = 9.7
    c: DistanceX(g-1,g0) = 12.9
    c: DistanceY(g-1,g0) = 16.5
FEATURE [PartDesign::Pocket] Pocket062  label="BearingPocket"
  BaseFeature = -> Pad015
  Direction = (0,-1,2e-16)
  Length = 5
  Length2 = 5
  Profile = -> Sketch070
  ReferenceAxis = -> Sketch070 [N_Axis]
  Suppressed = false
  Type = 0
FEATURE [Sketcher::SketchObject] Sketch071
  ArcFitTolerance = 1e-06
  AttachmentSupport = -> [Pocket062]
  FullyConstrained = true
  MakeInternals = false
  MapMode = 5
  Placement = pos=(0,1,0) rot=(0,0.707107,0.707107;3.14159rad)
  sketch-geometry (1):
    g0: Circle CenterX=12.9 CenterY=16.5 CenterZ=0 NormalX=0 NormalY=0 NormalZ=1 AngleXU=0 Radius=3.7625
  constraints (3):
    c: Diameter(g0) = 7.525
    c: DistanceY(g-1,g0) = 16.5
    c: DistanceX(g-1,g0) = 12.9
FEATURE [Sketcher::SketchObject] Sketch072
  ArcFitTolerance = 1e-06
  FullyConstrained = true
  MakeInternals = false
  MapMode = 5
  Placement = pos=(0,6,0) rot=(0,0.707107,0.707107;3.14159rad)
  sketch-geometry (1):
    g0: Circle CenterX=-20 CenterY=16.5 CenterZ=0 NormalX=0 NormalY=0 NormalZ=1 AngleXU=0 Radius=2.8
  constraints (3):
    c: Diameter(g0) = 5.6
    c: DistanceX(g0,g-1) = 20
    c: DistanceY(g-1,g0) = 16.5
FEATURE [PartDesign::Pocket] Pocket063  label="BearingHole"
  BaseFeature = -> Pocket062
  Direction = (0,-1,2e-16)
  Length = 5
  Length2 = 5
  Profile = -> Sketch071
  ReferenceAxis = -> Sketch071 [N_Axis]
  Suppressed = false
  Type = 1
FEATURE [PartDesign::Pocket] Pocket064  label="GuidePocket"
  BaseFeature = -> Pocket063
  Direction = (0,-1,2e-16)
  Length = 5
  Length2 = 5
  Profile = -> Sketch072
  ReferenceAxis = -> Sketch072 [N_Axis]
  Suppressed = false
  Type = 0
FEATURE [PartDesign::Body] Body006  label="EdgeMountBottomBody"
  AllowCompound = false
  Group = -> [Sketch067,Pad014,Sketch068,Pocket061,Sketch069,Pad015,Sketch070,Pocket062,Sketch071,Sketch072,Pocket063,Pocket064]
  Origin = -> Origin013
  Tip = -> Pocket064
FEATURE [App::Part] Part006  label="EdgeMountBottom"
  Group = -> [Body006]
  Origin = -> Origin012
FEATURE [Sketcher::SketchObject] Sketch075
  ArcFitTolerance = 1e-06
  FullyConstrained = true
  MakeInternals = false
  MapMode = 5
  Placement = pos=(0,0,4) rot=(0,0,1;0rad)
  sketch-geometry (1):
    g0: Circle CenterX=12.9 CenterY=12.185 CenterZ=0 NormalX=0 NormalY=0 NormalZ=1 AngleXU=0 Radius=3.7
  constraints (3):
    c: Diameter(g0) = 7.4
    c: DistanceX(g-1,g0) = 12.9
    c: DistanceY(g-1,g0) = 12.185
FEATURE [Sketcher::SketchObject] Sketch076
  ArcFitTolerance = 1e-06
  FullyConstrained = true
  MakeInternals = false
  MapMode = 5
  Placement = pos=(0,2.5,0) rot=(0,0.707107,0.707107;3.14159rad)
  sketch-geometry (4):
    g0: Circle CenterX=-19 CenterY=-10 CenterZ=0 NormalX=0 NormalY=0 NormalZ=1 AngleXU=0 Radius=1.6
    g1: Circle CenterX=19 CenterY=-10 CenterZ=0 NormalX=0 NormalY=0 NormalZ=1 AngleXU=0 Radius=1.6
    g2: Circle CenterX=19 CenterY=-31.575 CenterZ=0 NormalX=0 NormalY=0 NormalZ=1 AngleXU=0 Radius=1.6
    g3: Circle CenterX=-19 CenterY=-31.575 CenterZ=0 NormalX=0 NormalY=0 NormalZ=1 AngleXU=0 Radius=1.6
  constraints (12):
    c: Equal(g0,g1)
    c: Equal(g0,g2)
    c: Equal(g0,g3)
    c: Diameter(g0) = 3.2
    c: DistanceY(g1,g0) = 0
    c: DistanceY(g2,g3) = 0
    c: DistanceX(g0,g3) = 0
    c: DistanceX(g1,g2) = 0
    c: DistanceY(g1,g-1) = 10
    c: DistanceY(g2,g-1) = 31.575
    c: DistanceX(g0,g-1) = 19
    c: DistanceX(g-1,g1) = 19
FEATURE [Sketcher::SketchObject] Sketch077
  ArcFitTolerance = 1e-06
  FullyConstrained = true
  MakeInternals = false
  MapMode = 5
  Placement = pos=(0,2.5,0) rot=(0,0.707107,0.707107;3.14159rad)
  sketch-geometry (4):
    g0: LineSegment StartX=-25.4 StartY=-22 StartZ=0 EndX=-25.4 EndY=-28 EndZ=0
    g1: LineSegment StartX=-25.4 StartY=-28 StartZ=0 EndX=25.4 EndY=-28 EndZ=0
    g2: LineSegment StartX=25.4 StartY=-28 StartZ=0 EndX=25.4 EndY=-22 EndZ=0
    g3: LineSegment StartX=25.4 StartY=-22 StartZ=0 EndX=-25.4 EndY=-22 EndZ=0
  constraints (12):
    c: Coincident(g0,g1)
    c: Coincident(g1,g2)
    c: Coincident(g2,g3)
    c: Coincident(g3,g0)
    c: Vertical(g0)
    c: Vertical(g2)
    c: Horizontal(g1)
    c: Horizontal(g3)
    c: Distance(g0,g2) = 50.8
    c: Distance(g1,g3) = 6
    c: DistanceX(g-1,g2) = 25.4
    c: DistanceY(g0,g-1) = 22
FEATURE [Sketcher::SketchObject] Sketch081
  ArcFitTolerance = 1e-06
  FullyConstrained = true
  MakeInternals = false
  MapMode = 5
  Placement = pos=(0,0,4) rot=(0,0,1;0rad)
  sketch-geometry (2):
    g0: Circle CenterX=4.4 CenterY=12.185 CenterZ=0 NormalX=0 NormalY=0 NormalZ=1 AngleXU=0 Radius=1.6
    g1: Circle CenterX=21.4 CenterY=12.185 CenterZ=0 NormalX=0 NormalY=0 NormalZ=1 AngleXU=0 Radius=1.6
  constraints (6):
    c: Equal(g0,g1)
    c: Diameter(g0) = 3.2
    c: DistanceY(g0,g1) = 0
    c: DistanceY(g-1,g0) = 12.185
    c: DistanceX(g0,g1) = 17
    c: DistanceX(g-1,g1) = 21.4
FEATURE [Sketcher::SketchObject] Sketch073
  ArcFitTolerance = 1e-06
  AttachmentSupport = -> [XY_Plane015]
  FullyConstrained = true
  MakeInternals = false
  MapMode = 5
  sketch-geometry (7):
    g0: LineSegment StartX=-25.4 StartY=2.5 StartZ=0 EndX=-25.4 EndY=-10 EndZ=0
    g1: LineSegment StartX=-25.4 StartY=-10 StartZ=0 EndX=25.4 EndY=-10 EndZ=0
    g2: LineSegment StartX=25.4 StartY=-10 StartZ=0 EndX=25.4 EndY=2.5 EndZ=0
    g3: LineSegment StartX=0.4 StartY=2.5 StartZ=0 EndX=-25.4 EndY=2.5 EndZ=0
    g4: LineSegment StartX=0.4 StartY=2.5 StartZ=0 EndX=0.4 EndY=12.185 EndZ=0
    g5: LineSegment StartX=25.4 StartY=2.5 StartZ=0 EndX=25.4 EndY=12.185 EndZ=0
    g6: ArcOfCircle CenterX=12.9 CenterY=12.185 CenterZ=0 NormalX=0 NormalY=0 NormalZ=1 AngleXU=0 Radius=12.5 StartAngle=0 EndAngle=3.14159
  constraints (22):
    c: Vertical(g0)
    c: Coincident(g0,g1)
    c: Horizontal(g1)
    c: Coincident(g1,g2)
    c: Vertical(g2)
    c: Coincident(g3,g0)
    c: Horizontal(g3)
    c: DistanceX(g1,g1) = 50.8
    c: DistanceX(g-1,g1) = 25.4
    c: DistanceY(g0,g0) = 12.5
    c: DistanceY(g-1,g0) = 2.5
    c: DistanceX(g3,g1) = 25
    c: DistanceY(g2,g2) = 12.5
    c: Coincident(g4,g3)
    c: Vertical(g4)
    c: Coincident(g5,g2)
    c: Vertical(g5)
    c: Coincident(g6,g5)
    c: Coincident(g6,g4)
    c: DistanceY(g-1,g6) = 12.185
    c: DistanceY(g5,g6) = 0
    c: DistanceY(g4,g6) = 0
FEATURE [PartDesign::Pad] Pad016  label="MainPad001"
  Direction = (0,0,1)
  Length = 4
  Length2 = 10
  Profile = -> Sketch073
  ReferenceAxis = -> Sketch073 [N_Axis]
  Suppressed = false
  Type = 0
FEATURE [Sketcher::SketchObject] Sketch074
  ArcFitTolerance = 1e-06
  AttachmentSupport = -> [Pad016]
  FullyConstrained = true
  MakeInternals = false
  MapMode = 5
  Placement = pos=(0,0,0) rot=(1,0,0;3.14159rad)
  sketch-geometry (4):
    g0: LineSegment StartX=-25.4 StartY=0 StartZ=0 EndX=-25.4 EndY=-2.5 EndZ=0
    g1: LineSegment StartX=-25.4 StartY=-2.5 StartZ=0 EndX=25.4 EndY=-2.5 EndZ=0
    g2: LineSegment StartX=25.4 StartY=-2.5 StartZ=0 EndX=25.4 EndY=0 EndZ=0
    g3: LineSegment StartX=25.4 StartY=0 StartZ=0 EndX=-25.4 EndY=0 EndZ=0
  constraints (12):
    c: Coincident(g0,g1)
    c: Coincident(g1,g2)
    c: Coincident(g2,g3)
    c: Coincident(g3,g0)
    c: Vertical(g0)
    c: Vertical(g2)
    c: Horizontal(g1)
    c: Horizontal(g3)
    c: Distance(g0,g2) = 50.8
    c: Distance(g1,g3) = 2.5
    c: DistanceX(g0,g-1) = 25.4
    c: DistanceY(g0,g-1) = 0
FEATURE [PartDesign::Pad] Pad017  label="EdgePad005"
  BaseFeature = -> Pad016
  Direction = (0,0,-1)
  Length = 36.1
  Length2 = 10
  Profile = -> Sketch074
  ReferenceAxis = -> Sketch074 [N_Axis]
  Suppressed = false
  Type = 0
FEATURE [Sketcher::SketchObject] Sketch082
  ArcFitTolerance = 1e-06
  AttachmentSupport = -> [Pad017]
  FullyConstrained = true
  MakeInternals = false
  MapMode = 5
  Placement = pos=(0,0,0) rot=(1,0,0;3.14159rad)
  sketch-geometry (4):
    g0: LineSegment StartX=-25.4 StartY=0 StartZ=0 EndX=25.4 EndY=0 EndZ=0
    g1: LineSegment StartX=25.4 StartY=0 StartZ=0 EndX=25.4 EndY=10 EndZ=0
    g2: LineSegment StartX=25.4 StartY=10 StartZ=0 EndX=-25.4 EndY=10 EndZ=0
    g3: LineSegment StartX=-25.4 StartY=10 StartZ=0 EndX=-25.4 EndY=0 EndZ=0
  constraints (12):
    c: Coincident(g0,g1)
    c: Coincident(g1,g2)
    c: Coincident(g2,g3)
    c: Coincident(g3,g0)
    c: Horizontal(g0)
    c: Horizontal(g2)
    c: Vertical(g1)
    c: Vertical(g3)
    c: PointOnObject(g0,g-1)
    c: DistanceY(g1,g1) = 10
    c: DistanceX(g2,g2) = 50.8
    c: DistanceX(g-1,g1) = 25.4
FEATURE [PartDesign::Pad] Pad018  label="BackPad"
  BaseFeature = -> Pad017
  Direction = (0,0,-1)
  Length = 5.5
  Length2 = 10
  Profile = -> Sketch082
  ReferenceAxis = -> Sketch082 [N_Axis]
  Suppressed = false
  Type = 0
FEATURE [PartDesign::Pocket] Pocket065  label="MotorRingPocket"
  BaseFeature = -> Pad018
  Direction = (0,0,-1)
  Length = 5
  Length2 = 5
  Profile = -> Sketch075
  ReferenceAxis = -> Sketch075 [N_Axis]
  Suppressed = false
  Type = 0
FEATURE [PartDesign::Pocket] Pocket066  label="EdgeScrewPockets002"
  BaseFeature = -> Pocket065
  Direction = (-1e-16,-1,2e-16)
  Length = 5
  Length2 = 5
  Profile = -> Sketch076
  ReferenceAxis = -> Sketch076 [N_Axis]
  Suppressed = false
  Type = 0
FEATURE [PartDesign::Pad] Pad019  label="BearingPad"
  BaseFeature = -> Pocket066
  Direction = (1e-16,1,-2e-16)
  Length = 19.27
  Length2 = 10
  Profile = -> Sketch077
  ReferenceAxis = -> Sketch077 [N_Axis]
  Suppressed = false
  Type = 0
FEATURE [Sketcher::SketchObject] Sketch078
  ArcFitTolerance = 1e-06
  AttachmentSupport = -> [Pad019]
  FullyConstrained = true
  MakeInternals = false
  MapMode = 5
  Placement = pos=(2.5e-15,-6.2e-15,-28) rot=(1,0,0;3.14159rad)
  sketch-geometry (1):
    g0: Circle CenterX=12.9 CenterY=-12.185 CenterZ=0 NormalX=0 NormalY=0 NormalZ=1 AngleXU=0 Radius=6.585
  constraints (3):
    c: Diameter(g0) = 13.17
    c: DistanceY(g-1,g0) = -12.185
    c: DistanceX(g-1,g0) = 12.9
FEATURE [PartDesign::Pocket] Pocket067  label="BearingPocket001"
  BaseFeature = -> Pad019
  Direction = (0,0,1)
  Length = 5.1625
  Length2 = 5
  Profile = -> Sketch078
  ReferenceAxis = -> Sketch078 [N_Axis]
  Suppressed = false
  Type = 0
FEATURE [Sketcher::SketchObject] Sketch079
  ArcFitTolerance = 1e-06
  AttachmentSupport = -> [Pocket067]
  FullyConstrained = true
  MakeInternals = false
  MapMode = 5
  Placement = pos=(0,0,-22.8375) rot=(1,0,0;3.14159rad)
  sketch-geometry (1):
    g0: Circle CenterX=12.9 CenterY=-12.185 CenterZ=0 NormalX=0 NormalY=0 NormalZ=1 AngleXU=0 Radius=5.25
  constraints (3):
    c: Diameter(g0) = 10.5
    c: DistanceY(g0,g-1) = 12.185
    c: DistanceX(g-1,g0) = 12.9
FEATURE [PartDesign::Pocket] Pocket068  label="ShaftPocket"
  BaseFeature = -> Pocket067
  Direction = (0,0,1)
  Length = 5
  Length2 = 5
  Profile = -> Sketch079
  ReferenceAxis = -> Sketch079 [N_Axis]
  Suppressed = false
  Type = 0
FEATURE [Sketcher::SketchObject] Sketch080
  ArcFitTolerance = 1e-06
  AttachmentSupport = -> [Pocket068]
  FullyConstrained = true
  MakeInternals = false
  MapMode = 5
  Placement = pos=(2.5e-15,-6.2e-15,-28) rot=(1,0,0;3.14159rad)
  sketch-geometry (1):
    g0: Circle CenterX=-19.9 CenterY=-12.185 CenterZ=0 NormalX=0 NormalY=0 NormalZ=1 AngleXU=0 Radius=2.75
  constraints (3):
    c: Diameter(g0) = 5.5
    c: DistanceY(g0,g-1) = 12.185
    c: DistanceX(g0,g-1) = 19.9
FEATURE [PartDesign::Pocket] Pocket069  label="GuidePocket001"
  BaseFeature = -> Pocket068
  Direction = (0,0,1)
  Length = 4
  Length2 = 5
  Profile = -> Sketch080
  ReferenceAxis = -> Sketch080 [N_Axis]
  Suppressed = false
  Type = 0
FEATURE [PartDesign::Pocket] Pocket070
  BaseFeature = -> Pocket069
  Direction = (0,0,-1)
  Length = 5
  Length2 = 5
  Profile = -> Sketch081
  ReferenceAxis = -> Sketch081 [N_Axis]
  Suppressed = false
  Type = 0
FEATURE [PartDesign::Chamfer] Chamfer010
  Angle = 45
  Base = -> Pocket070 [Edge53,Edge52,Edge33,Edge32]
  BaseFeature = -> Pocket070
  ChamferType = 0
  FlipDirection = false
  Size = 1.8
  Size2 = 1
  SupportTransform = false
  Suppressed = false
  UseAllEdges = false
FEATURE [PartDesign::Chamfer] Chamfer011
  Angle = 45
  Base = -> Chamfer010 [Edge80,Edge81]
  BaseFeature = -> Chamfer010
  ChamferType = 0
  FlipDirection = false
  Size = 1
  Size2 = 1
  SupportTransform = false
  Suppressed = false
  UseAllEdges = false
FEATURE [PartDesign::Chamfer] Chamfer012
  Angle = 45
  Base = -> Chamfer011 [Edge78,Edge76]
  BaseFeature = -> Chamfer011
  ChamferType = 0
  FlipDirection = false
  Size = 1.5
  Size2 = 1
  SupportTransform = false
  Suppressed = false
  UseAllEdges = false
FEATURE [PartDesign::Fillet] Fillet001
  Base = -> Chamfer012 [Edge64,Edge77]
  BaseFeature = -> Chamfer012
  Radius = 10
  SupportTransform = false
  Suppressed = false
  UseAllEdges = false
FEATURE [PartDesign::Body] Body007  label="MotorMountBody"
  AllowCompound = false
  Group = -> [Sketch073,Pad016,Sketch074,Sketch075,Sketch076,Sketch077,Sketch078,Sketch079,Sketch080,Sketch081,Pad017,Sketch082,Pad018,Pocket065,Pocket066,Pad019,Pocket067,Pocket068,Pocket069,Pocket070,Chamfer010,Chamfer011,Chamfer012,Fillet001]
  Origin = -> Origin015
  Tip = -> Fillet001
FEATURE [Sketcher::SketchObject] Sketch083
  ArcFitTolerance = 1e-06
  AttachmentOffset = pos=(0,0,-21.99) rot=(0,0,1;0rad)
  AttachmentSupport = -> [XY_Plane016]
  FullyConstrained = true
  MakeInternals = false
  MapMode = 5
  Placement = pos=(0,0,-21.99) rot=(0,0,1;0rad)
  sketch-geometry (4):
    g0: LineSegment StartX=-26.171 StartY=25.7025 StartZ=0 EndX=-26.171 EndY=-25.7025 EndZ=0
    g1: LineSegment StartX=-26.171 StartY=-25.7025 StartZ=0 EndX=26.171 EndY=-25.7025 EndZ=0
    g2: LineSegment StartX=26.171 StartY=-25.7025 StartZ=0 EndX=26.171 EndY=25.7025 EndZ=0
    g3: LineSegment StartX=26.171 StartY=25.7025 StartZ=0 EndX=-26.171 EndY=25.7025 EndZ=0
  constraints (11):
    c: Coincident(g0,g1)
    c: Coincident(g1,g2)
    c: Coincident(g2,g3)
    c: Coincident(g3,g0)
    c: Vertical(g0)
    c: Vertical(g2)
    c: Horizontal(g1)
    c: Horizontal(g3)
    c: Symmetric(g2,g0,g-1)
    c: DistanceX(g3,g3) = 52.342
    c: DistanceY(g2,g2) = 51.405
FEATURE [PartDesign::Pad] Pad020
  Direction = (0,0,1)
  Length = 0.01
  Length2 = 10
  Profile = -> Sketch083
  ReferenceAxis = -> Sketch083 [N_Axis]
  Suppressed = false
  Type = 0
FEATURE [PartDesign::Body] Body008  label="Slice"
  AllowCompound = false
  Group = -> [Sketch083,Pad020]
  Origin = -> Origin016
  Tip = -> Pad020
FEATURE [App::Part] Part007  label="MotorMountPart"
  Group = -> [Body007,Body008]
  Origin = -> Origin014
FEATURE [Part::Feature] Solid  label="BearingHolder"
  shape: bbox 50.8 x 21.77 x 14.11 mm, 25 faces (baked)
FEATURE [Part::Feature] Solid001
  shape: bbox 50.8 x 2.5 x 0.01 mm, 6 faces (baked)
FEATURE [Part::Feature] Solid002  label="MotorMount"
  shape: bbox 50.8 x 34.69 x 25.98 mm, 27 faces (baked)
FEATURE [Sketcher::SketchObject] Sketch084
  ArcFitTolerance = 1e-06
  AttachmentSupport = -> [XY_Plane018]
  FullyConstrained = true
  MakeInternals = false
  MapMode = 5
  sketch-geometry (4):
    g0: LineSegment StartX=-25.4 StartY=15.3 StartZ=0 EndX=-25.4 EndY=-15.3 EndZ=0
    g1: LineSegment StartX=-25.4 StartY=-15.3 StartZ=0 EndX=25.4 EndY=-15.3 EndZ=0
    g2: LineSegment StartX=25.4 StartY=-15.3 StartZ=0 EndX=25.4 EndY=15.3 EndZ=0
    g3: LineSegment StartX=25.4 StartY=15.3 StartZ=0 EndX=-25.4 EndY=15.3 EndZ=0
  constraints (11):
    c: Coincident(g0,g1)
    c: Coincident(g1,g2)
    c: Coincident(g2,g3)
    c: Coincident(g3,g0)
    c: Vertical(g0)
    c: Vertical(g2)
    c: Horizontal(g1)
    c: Horizontal(g3)
    c: Symmetric(g2,g0,g-1)
    c: DistanceX(g3,g3) = 50.8
    c: DistanceY(g2,g2) = 30.6
FEATURE [PartDesign::Pad] Pad021  label="Basepad"
  Direction = (0,0,1)
  Length = 2.5
  Length2 = 10
  Profile = -> Sketch084
  ReferenceAxis = -> Sketch084 [N_Axis]
  Suppressed = false
  Type = 0
FEATURE [Sketcher::SketchObject] Sketch085
  ArcFitTolerance = 1e-06
  AttachmentSupport = -> [Pad021]
  FullyConstrained = true
  MakeInternals = false
  MapMode = 5
  Placement = pos=(0,0,0) rot=(1,0,0;3.14159rad)
  sketch-geometry (4):
    g0: Circle CenterX=-19 CenterY=10.775 CenterZ=0 NormalX=0 NormalY=0 NormalZ=1 AngleXU=0 Radius=1.6
    g1: Circle CenterX=19 CenterY=10.775 CenterZ=0 NormalX=0 NormalY=0 NormalZ=1 AngleXU=0 Radius=1.6
    g2: Circle CenterX=19 CenterY=-10.8 CenterZ=0 NormalX=0 NormalY=0 NormalZ=1 AngleXU=0 Radius=1.6
    g3: Circle CenterX=-19 CenterY=-10.8 CenterZ=0 NormalX=0 NormalY=0 NormalZ=1 AngleXU=0 Radius=1.6
  constraints (12):
    c: Equal(g0,g1)
    c: Equal(g0,g2)
    c: Equal(g0,g3)
    c: Diameter(g0) = 3.2
    c: DistanceX(g0,g3) = 0
    c: DistanceX(g1,g2) = 0
    c: DistanceY(g1,g0) = 0
    c: DistanceY(g2,g3) = 0
    c: DistanceY(g2,g1) = 21.575
    c: DistanceX(g0,g-1) = 19
    c: DistanceX(g-1,g1) = 19
    c: DistanceY(g2,g-1) = 10.8
FEATURE [PartDesign::Pocket] Pocket071
  BaseFeature = -> Pad021
  Direction = (0,0,1)
  Length = 5
  Length2 = 5
  Profile = -> Sketch085
  ReferenceAxis = -> Sketch085 [N_Axis]
  Suppressed = false
  Type = 1
FEATURE [Sketcher::SketchObject] Sketch086
  ArcFitTolerance = 1e-06
  AttachmentSupport = -> [Pocket071]
  FullyConstrained = true
  MakeInternals = false
  MapMode = 5
  Placement = pos=(0,0,0) rot=(1,0,0;3.14159rad)
  sketch-geometry (4):
    g0: LineSegment StartX=-25.4 StartY=0 StartZ=0 EndX=-25.4 EndY=-6 EndZ=0
    g1: LineSegment StartX=-25.4 StartY=-6 StartZ=0 EndX=25.4 EndY=-6 EndZ=0
    g2: LineSegment StartX=25.4 StartY=-6 StartZ=0 EndX=25.4 EndY=0 EndZ=0
    g3: LineSegment StartX=25.4 StartY=0 StartZ=0 EndX=-25.4 EndY=0 EndZ=0
  constraints (12):
    c: Coincident(g0,g1)
    c: Coincident(g1,g2)
    c: Coincident(g2,g3)
    c: Coincident(g3,g0)
    c: Vertical(g0)
    c: Vertical(g2)
    c: Horizontal(g1)
    c: Horizontal(g3)
    c: DistanceX(g3,g3) = 50.8
    c: DistanceY(g0,g0) = 6
    c: DistanceX(g0,g-1) = 25.4
    c: DistanceY(g1,g-1) = 6
FEATURE [PartDesign::Pad] Pad022  label="BearingPad001"
  BaseFeature = -> Pocket071
  Direction = (0,0,-1)
  Length = 19.27
  Length2 = 10
  Profile = -> Sketch086
  ReferenceAxis = -> Sketch086 [N_Axis]
  Suppressed = false
  Type = 0
FEATURE [Sketcher::SketchObject] Sketch087
  ArcFitTolerance = 1e-06
  AttachmentSupport = -> [Pad022]
  FullyConstrained = true
  MakeInternals = false
  MapMode = 5
  Placement = pos=(0,0,0) rot=(1,0,0;1.5708rad)
  sketch-geometry (1):
    g0: Circle CenterX=-12.9 CenterY=-9.685 CenterZ=0 NormalX=0 NormalY=0 NormalZ=1 AngleXU=0 Radius=6.585
  constraints (3):
    c: Diameter(g0) = 13.17
    c: DistanceX(g0,g-1) = 12.9
    c: DistanceY(g0,g-1) = 9.685
FEATURE [PartDesign::Pocket] Pocket072  label="BearingPocket002"
  BaseFeature = -> Pad022
  Direction = (0,1,-2e-16)
  Length = 5
  Length2 = 5
  Profile = -> Sketch087
  ReferenceAxis = -> Sketch087 [N_Axis]
  Suppressed = false
  Type = 0
FEATURE [Sketcher::SketchObject] Sketch088
  ArcFitTolerance = 1e-06
  AttachmentSupport = -> [Pocket072]
  FullyConstrained = true
  MakeInternals = false
  MapMode = 5
  Placement = pos=(0,0,0) rot=(1,0,0;1.5708rad)
  sketch-geometry (1):
    g0: Circle CenterX=19.9 CenterY=-9.685 CenterZ=0 NormalX=0 NormalY=0 NormalZ=1 AngleXU=0 Radius=2.75
  constraints (3):
    c: Diameter(g0) = 5.5
    c: DistanceX(g-1,g0) = 19.9
    c: DistanceY(g0,g-1) = 9.685
FEATURE [PartDesign::Pocket] Pocket073  label="GuidePocket002"
  BaseFeature = -> Pocket072
  Direction = (0,1,-2e-16)
  Length = 4
  Length2 = 5
  Profile = -> Sketch088
  ReferenceAxis = -> Sketch088 [N_Axis]
  Suppressed = false
  Type = 0
FEATURE [Sketcher::SketchObject] Sketch089
  ArcFitTolerance = 1e-06
  AttachmentSupport = -> [Pocket073]
  FullyConstrained = true
  MakeInternals = false
  MapMode = 5
  Placement = pos=(0,5,0) rot=(1,0,0;1.5708rad)
  sketch-geometry (1):
    g0: Circle CenterX=-12.9 CenterY=-9.685 CenterZ=0 NormalX=0 NormalY=0 NormalZ=1 AngleXU=0 Radius=5.25
  constraints (3):
    c: Diameter(g0) = 10.5
    c: DistanceX(g0,g-1) = 12.9
    c: DistanceY(g0,g-1) = 9.685
FEATURE [PartDesign::Pocket] Pocket074
  BaseFeature = -> Pocket073
  Direction = (0,1,-2e-16)
  Length = 5
  Length2 = 5
  Profile = -> Sketch089
  ReferenceAxis = -> Sketch089 [N_Axis]
  Suppressed = false
  Type = 1
FEATURE [PartDesign::Chamfer] Chamfer013
  Angle = 45
  Base = -> Pocket074 [Edge22,Edge23,Edge16,Edge15]
  BaseFeature = -> Pocket074
  ChamferType = 0
  FlipDirection = false
  Size = 1.5
  Size2 = 1
  SupportTransform = false
  Suppressed = false
  UseAllEdges = false
FEATURE [PartDesign::Fillet] Fillet002
  Base = -> Chamfer013 [Edge50,Edge49]
  BaseFeature = -> Chamfer013
  Radius = 1
  SupportTransform = false
  Suppressed = false
  UseAllEdges = false
FEATURE [PartDesign::Fillet] Fillet003
  Base = -> Fillet002 [Edge17,Edge11]
  BaseFeature = -> Fillet002
  Radius = 10
  SupportTransform = false
  Suppressed = false
  UseAllEdges = false
FEATURE [PartDesign::Body] Body009  label="BottomMountBody"
  AllowCompound = false
  Group = -> [Sketch084,Pad021,Sketch085,Pocket071,Sketch086,Pad022,Sketch087,Pocket072,Sketch088,Pocket073,Sketch089,Pocket074,Chamfer013,Fillet002,Fillet003]
  Origin = -> Origin018
  Tip = -> Fillet003
FEATURE [App::Part] Part008  label="BottomMount"
  Group = -> [Body009]
  Origin = -> Origin017
FEATURE [Sketcher::SketchObject] Sketch090
  ArcFitTolerance = 1e-06
  AttachmentSupport = -> [XY_Plane020]
  FullyConstrained = true
  MakeInternals = false
  MapMode = 5
  sketch-geometry (4):
    g0: LineSegment StartX=-25.4 StartY=0 StartZ=0 EndX=-25.4 EndY=-27.7 EndZ=0
    g1: LineSegment StartX=-25.4 StartY=-27.7 StartZ=0 EndX=25.4 EndY=-27.7 EndZ=0
    g2: LineSegment StartX=25.4 StartY=-27.7 StartZ=0 EndX=25.4 EndY=0 EndZ=0
    g3: LineSegment StartX=25.4 StartY=0 StartZ=0 EndX=-25.4 EndY=0 EndZ=0
  constraints (12):
    c: Coincident(g0,g1)
    c: Coincident(g1,g2)
    c: Coincident(g2,g3)
    c: Coincident(g3,g0)
    c: Vertical(g0)
    c: Vertical(g2)
    c: Horizontal(g1)
    c: Horizontal(g3)
    c: Distance(g0,g2) = 50.8
    c: Distance(g1,g3) = 27.7
    c: DistanceY(g-1,g0) = 0
    c: DistanceX(g0,g-1) = 25.4
FEATURE [PartDesign::Pad] Pad023  label="BodyPad"
  Direction = (0,0,1)
  Length = 9.2
  Length2 = 10
  Profile = -> Sketch090
  ReferenceAxis = -> Sketch090 [N_Axis]
  Suppressed = false
  Type = 0
FEATURE [Sketcher::SketchObject] Sketch091
  ArcFitTolerance = 1e-06
  AttachmentSupport = -> [Pad023]
  FullyConstrained = true
  MakeInternals = false
  MapMode = 5
  Placement = pos=(0,-27.7,0) rot=(1,0,0;1.5708rad)
  sketch-geometry (4):
    g0: LineSegment StartX=-3 StartY=7.5 StartZ=0 EndX=-3 EndY=1.5 EndZ=0
    g1: LineSegment StartX=-3 StartY=1.5 StartZ=0 EndX=3 EndY=1.5 EndZ=0
    g2: LineSegment StartX=3 StartY=1.5 StartZ=0 EndX=3 EndY=7.5 EndZ=0
    g3: LineSegment StartX=3 StartY=7.5 StartZ=0 EndX=-3 EndY=7.5 EndZ=0
  constraints (12):
    c: Coincident(g0,g1)
    c: Coincident(g1,g2)
    c: Coincident(g2,g3)
    c: Coincident(g3,g0)
    c: Vertical(g0)
    c: Vertical(g2)
    c: Horizontal(g1)
    c: Horizontal(g3)
    c: Distance(g0,g2) = 6
    c: Distance(g1,g3) = 6
    c: DistanceX(g0,g-1) = 3
    c: DistanceY(g-1,g0) = 1.5
FEATURE [PartDesign::Pocket] Pocket075  label="BrushSquare"
  BaseFeature = -> Pad023
  Direction = (0,1,-2e-16)
  Length = 10.2
  Length2 = 5
  Profile = -> Sketch091
  ReferenceAxis = -> Sketch091 [N_Axis]
  Suppressed = false
  Type = 0
FEATURE [Sketcher::SketchObject] Sketch092
  ArcFitTolerance = 1e-06
  AttachmentSupport = -> [Pocket075]
  FullyConstrained = true
  MakeInternals = false
  MapMode = 5
  Placement = pos=(0,-17.5,0) rot=(1,0,0;1.5708rad)
  sketch-geometry (1):
    g0: Circle CenterX=0 CenterY=4.6 CenterZ=0 NormalX=0 NormalY=0 NormalZ=1 AngleXU=0 Radius=3
  constraints (3):
    c: Diameter(g0) = 6
    c: PointOnObject(g0,g-2)
    c: DistanceY(g-1,g0) = 4.6
FEATURE [PartDesign::Pocket] Pocket076  label="BrushSpringPocket"
  BaseFeature = -> Pocket075
  Direction = (0,1,-2e-16)
  Length = 11
  Length2 = 5
  Profile = -> Sketch092
  ReferenceAxis = -> Sketch092 [N_Axis]
  Suppressed = false
  Type = 0
FEATURE [Sketcher::SketchObject] Sketch093
  ArcFitTolerance = 1e-06
  AttachmentSupport = -> [Pocket076]
  FullyConstrained = false
  MakeInternals = false
  MapMode = 5
  Placement = pos=(-25.4,0,0) rot=(0.57735,-0.57735,-0.57735;2.0944rad)
  sketch-geometry (7):
    g0: LineSegment StartX=6.65774 StartY=6.02926 StartZ=0 EndX=4.21609 EndY=7.39979 EndZ=0
    g1: LineSegment StartX=4.21609 StartY=7.39979 StartZ=0 EndX=1.80835 EndY=5.97053 EndZ=0
    g2: LineSegment StartX=1.80835 StartY=5.97053 StartZ=0 EndX=1.84226 EndY=3.17074 EndZ=0
    g3: LineSegment StartX=1.84226 StartY=3.17074 StartZ=0 EndX=4.28391 EndY=1.80021 EndZ=0
    g4: LineSegment StartX=4.28391 StartY=1.80021 StartZ=0 EndX=6.69165 EndY=3.22947 EndZ=0
    g5: LineSegment StartX=6.69165 StartY=3.22947 StartZ=0 EndX=6.65774 EndY=6.02926 EndZ=0
    g6: Circle [constr] CenterX=4.25 CenterY=4.6 CenterZ=0 NormalX=0 NormalY=0 NormalZ=1 AngleXU=0 Radius=2.8
  constraints (16):
    c: Coincident(g0,g1)
    c: Coincident(g1,g2)
    c: Coincident(g2,g3)
    c: Coincident(g3,g4)
    c: Coincident(g4,g5)
    c: Coincident(g5,g0)
    c: Equal(g0, g1-g5) x5
    c: PointOnObject(g0,g6)
    c: PointOnObject(g1,g6)
    c: PointOnObject(g2,g6)
    c: PointOnObject(g3,g6)
    c: PointOnObject(g4,g6)
    c: PointOnObject(g5,g6)
    c: Radius(g6) = 2.8
    c: DistanceX(g-1,g6) = 4.25
    c: DistanceY(g-1,g6) = 4.6
FEATURE [PartDesign::Pocket] Pocket077  label="HexSidePocket"
  BaseFeature = -> Pocket076
  Direction = (1,0,0)
  Length = 30.9
  Length2 = 5
  Profile = -> Sketch093
  ReferenceAxis = -> Sketch093 [N_Axis]
  Suppressed = false
  Type = 0
FEATURE [Sketcher::SketchObject] Sketch094
  ArcFitTolerance = 1e-06
  AttachmentSupport = -> [Pocket077]
  FullyConstrained = true
  MakeInternals = false
  MapMode = 5
  Placement = pos=(0,0,9.2) rot=(0,0,1;0rad)
  sketch-geometry (1):
    g0: Circle CenterX=19.9 CenterY=-17.515 CenterZ=0 NormalX=0 NormalY=0 NormalZ=1 AngleXU=0 Radius=2.85
  constraints (3):
    c: Diameter(g0) = 5.7
    c: DistanceX(g-1,g0) = 19.9
    c: DistanceY(g0,g-1) = 17.515
FEATURE [PartDesign::Pocket] Pocket078  label="GuidePocket003"
  BaseFeature = -> Pocket077
  Direction = (0,0,-1)
  Length = 5
  Length2 = 5
  Profile = -> Sketch094
  ReferenceAxis = -> Sketch094 [N_Axis]
  Suppressed = false
  Type = 1
FEATURE [Sketcher::SketchObject] Sketch095
  ArcFitTolerance = 1e-06
  AttachmentSupport = -> [Pocket078]
  FullyConstrained = true
  MakeInternals = false
  MapMode = 5
  Placement = pos=(0,0,9.2) rot=(0,0,1;0rad)
  sketch-geometry (7):
    g0: LineSegment StartX=-7.4 StartY=-18.015 StartZ=0 EndX=-10.15 EndY=-13.2519 EndZ=0
    g1: LineSegment StartX=-10.15 StartY=-13.2519 StartZ=0 EndX=-15.65 EndY=-13.2519 EndZ=0
    g2: LineSegment StartX=-15.65 StartY=-13.2519 StartZ=0 EndX=-18.4 EndY=-18.015 EndZ=0
    g3: LineSegment StartX=-18.4 StartY=-18.015 StartZ=0 EndX=-15.65 EndY=-22.7781 EndZ=0
    g4: LineSegment StartX=-15.65 StartY=-22.7781 StartZ=0 EndX=-10.15 EndY=-22.7781 EndZ=0
    g5: LineSegment StartX=-10.15 StartY=-22.7781 StartZ=0 EndX=-7.4 EndY=-18.015 EndZ=0
    g6: Circle [constr] CenterX=-12.9 CenterY=-18.015 CenterZ=0 NormalX=0 NormalY=0 NormalZ=1 AngleXU=0 Radius=5.5
  constraints (17):
    c: Coincident(g0,g1)
    c: Coincident(g1,g2)
    c: Coincident(g2,g3)
    c: Coincident(g3,g4)
    c: Coincident(g4,g5)
    c: Coincident(g5,g0)
    c: Equal(g0, g1-g5) x5
    c: PointOnObject(g0,g6)
    c: PointOnObject(g1,g6)
    c: PointOnObject(g2,g6)
    c: PointOnObject(g3,g6)
    c: PointOnObject(g4,g6)
    c: PointOnObject(g5,g6)
    c: Radius(g6) = 5.5
    c: DistanceX(g6,g-1) = 12.9
    c: DistanceY(g6,g-1) = 18.015
    c: DistanceY(g0,g-1) = 18.015
FEATURE [PartDesign::Pocket] Pocket079  label="QuarterHexPocket"
  BaseFeature = -> Pocket078
  Direction = (0,0,-1)
  Length = 5
  Length2 = 5
  Profile = -> Sketch095
  ReferenceAxis = -> Sketch095 [N_Axis]
  Suppressed = false
  Type = 1
FEATURE [Sketcher::SketchObject] Sketch096
  ArcFitTolerance = 1e-06
  AttachmentSupport = -> [Pocket079]
  FullyConstrained = true
  MakeInternals = false
  MapMode = 5
  Placement = pos=(0,-27.7,0) rot=(1,0,0;1.5708rad)
  sketch-geometry (4):
    g0: LineSegment StartX=-3.25 StartY=7.85 StartZ=0 EndX=-3.25 EndY=1.35 EndZ=0
    g1: LineSegment StartX=-3.25 StartY=1.35 StartZ=0 EndX=3.25 EndY=1.35 EndZ=0
    g2: LineSegment StartX=3.25 StartY=1.35 StartZ=0 EndX=3.25 EndY=7.85 EndZ=0
    g3: LineSegment StartX=3.25 StartY=7.85 StartZ=0 EndX=-3.25 EndY=7.85 EndZ=0
  constraints (12):
    c: Coincident(g0,g1)
    c: Coincident(g1,g2)
    c: Coincident(g2,g3)
    c: Coincident(g3,g0)
    c: Vertical(g0)
    c: Vertical(g2)
    c: Horizontal(g1)
    c: Horizontal(g3)
    c: Distance(g0,g2) = 6.5
    c: Distance(g1,g3) = 6.5
    c: DistanceX(g0,g-1) = 3.25
    c: DistanceY(g-1,g0) = 1.35
FEATURE [PartDesign::Pad] Pad024  label="TipPad"
  BaseFeature = -> Pocket079
  Direction = (0,-1,2e-16)
  Length = 1.75
  Length2 = 10
  Profile = -> Sketch096
  ReferenceAxis = -> Sketch096 [N_Axis]
  Suppressed = false
  Type = 0
FEATURE [Sketcher::SketchObject] Sketch097
  ArcFitTolerance = 1e-06
  AttachmentSupport = -> [Pad024]
  FullyConstrained = true
  MakeInternals = false
  MapMode = 5
  Placement = pos=(0,-29.45,0) rot=(1,0,0;1.5708rad)
  sketch-geometry (4):
    g0: LineSegment StartX=-2.6 StartY=7.2 StartZ=0 EndX=-2.6 EndY=2 EndZ=0
    g1: LineSegment StartX=-2.6 StartY=2 StartZ=0 EndX=2.6 EndY=2 EndZ=0
    g2: LineSegment StartX=2.6 StartY=2 StartZ=0 EndX=2.6 EndY=7.2 EndZ=0
    g3: LineSegment StartX=2.6 StartY=7.2 StartZ=0 EndX=-2.6 EndY=7.2 EndZ=0
  constraints (12):
    c: Coincident(g0,g1)
    c: Coincident(g1,g2)
    c: Coincident(g2,g3)
    c: Coincident(g3,g0)
    c: Vertical(g0)
    c: Vertical(g2)
    c: Horizontal(g1)
    c: Horizontal(g3)
    c: Distance(g0,g2) = 5.2
    c: Distance(g1,g3) = 5.2
    c: DistanceX(g-1,g1) = 2.6
    c: DistanceY(g-1,g0) = 7.2
FEATURE [PartDesign::Pocket] Pocket080
  BaseFeature = -> Pad024
  Direction = (0,1,-2e-16)
  Length = 1.75
  Length2 = 5
  Profile = -> Sketch097
  ReferenceAxis = -> Sketch097 [N_Axis]
  Suppressed = false
  Type = 0
FEATURE [PartDesign::Fillet] Fillet004
  Base = -> Pocket080 [Edge4,Edge32]
  BaseFeature = -> Pocket080
  Radius = 10
  SupportTransform = false
  Suppressed = false
  UseAllEdges = false
FEATURE [PartDesign::Fillet] Fillet005
  Base = -> Fillet004 [Edge25]
  BaseFeature = -> Fillet004
  Radius = 15
  SupportTransform = false
  Suppressed = false
  UseAllEdges = false
FEATURE [PartDesign::Fillet] Fillet006
  Base = -> Fillet005 [Edge16]
  BaseFeature = -> Fillet005
  Radius = 1.5
  SupportTransform = false
  Suppressed = false
  UseAllEdges = false
FEATURE [Sketcher::SketchObject] Sketch098
  ArcFitTolerance = 1e-06
  AttachmentSupport = -> [Fillet006]
  FullyConstrained = false
  MakeInternals = false
  MapMode = 5
  Placement = pos=(0,0,9.2) rot=(0,0,1;0rad)
  sketch-geometry (4):
    g0: LineSegment StartX=-29.0837 StartY=-26.4096 StartZ=0 EndX=-29.0837 EndY=-31.8815 EndZ=0
    g1: LineSegment StartX=-29.0837 StartY=-31.8815 StartZ=0 EndX=25.6973 EndY=-31.8815 EndZ=0
    g2: LineSegment StartX=25.6973 StartY=-31.8815 StartZ=0 EndX=25.6973 EndY=-26.4096 EndZ=0
    g3: LineSegment StartX=25.6973 StartY=-26.4096 StartZ=0 EndX=-29.0837 EndY=-26.4096 EndZ=0
  constraints (8):
    c: Coincident(g0,g1)
    c: Coincident(g1,g2)
    c: Coincident(g2,g3)
    c: Coincident(g3,g0)
    c: Vertical(g0)
    c: Vertical(g2)
    c: Horizontal(g1)
    c: Horizontal(g3)
FEATURE [PartDesign::Pocket] Pocket081
  BaseFeature = -> Fillet006
  Direction = (0,0,-1)
  Length = 5
  Length2 = 5
  Profile = -> Sketch098
  ReferenceAxis = -> Sketch098 [N_Axis]
  Refine = true
  Suppressed = false
  Type = 1
FEATURE [PartDesign::Chamfer] Chamfer014
  Angle = 45
  Base = -> Pocket081 [Edge54,Edge15]
  BaseFeature = -> Pocket081
  ChamferType = 0
  FlipDirection = false
  Refine = true
  Size = 1.5
  Size2 = 1
  SupportTransform = false
  Suppressed = false
  UseAllEdges = false
FEATURE [PartDesign::Fillet] Fillet007
  Base = -> Chamfer014 [Edge57,Edge17]
  BaseFeature = -> Chamfer014
  Radius = 2
  Refine = true
  SupportTransform = false
  Suppressed = false
  UseAllEdges = false
FEATURE [PartDesign::Body] Body010  label="BrushBody"
  AllowCompound = false
  Group = -> [Sketch090,Pad023,Sketch091,Pocket075,Sketch092,Pocket076,Sketch093,Pocket077,Sketch094,Pocket078,Sketch095,Pocket079,Sketch096,Pad024,Sketch097,Pocket080,Fillet004,Fillet005,Fillet006,Sketch098,Pocket081,Chamfer014,Fillet007]
  Origin = -> Origin020
  Tip = -> Fillet007
FEATURE [App::Part] Part009  label="Brush"
  Group = -> [Body010]
  Origin = -> Origin019
